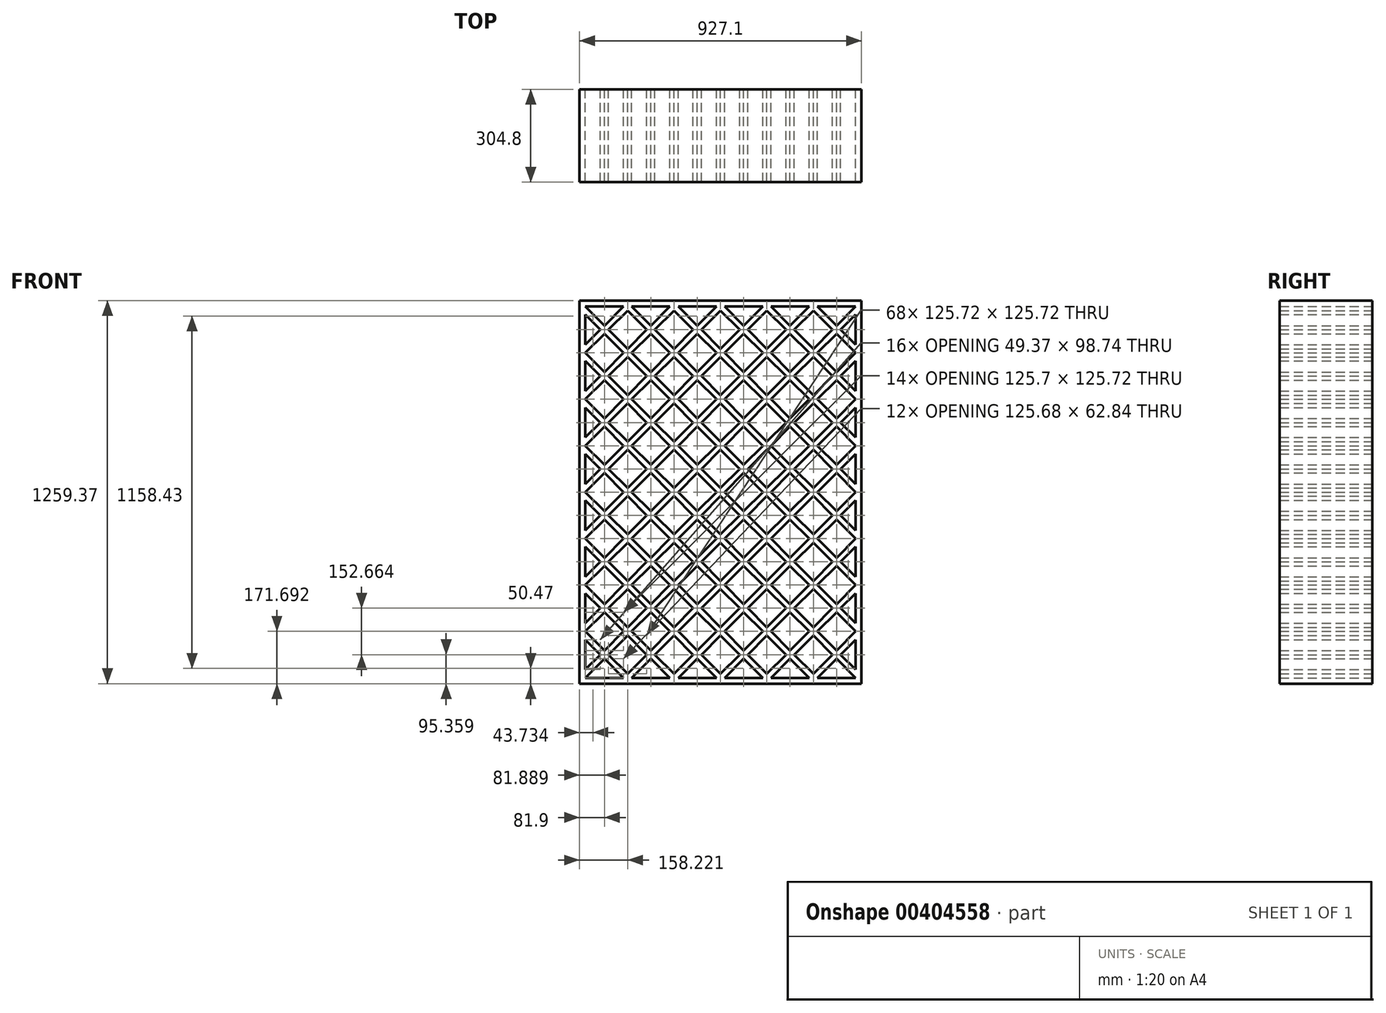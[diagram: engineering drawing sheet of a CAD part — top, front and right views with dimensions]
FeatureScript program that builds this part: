
annotation { "Feature Type Name" : "Feature", "Feature Type Description" : "" }
export const myFeature = defineFeature(function(context is Context, id is Id, definition is map)
    precondition{}
    {
        {
            var Q0;
            Q0=qCreatedBy(makeId("Front.planeOp"),FACE);
            var sketch = newSketch(context, id + "F0", { "sketchPlane" : qUnion([Q0])});
            skLineSegment(sketch, "E0.bottom", {"start": v(0, 0) * mm, "end": v(889, 0) * mm});
            skLineSegment(sketch, "E0.left", {"start": v(0, 0) * mm, "end": v(0, 1221.27) * mm});
            skLineSegment(sketch, "E0.right", {"start": v(889, 0) * mm, "end": v(889, 1221.27) * mm});
            skLineSegment(sketch, "E1", {"start": v(0, 0) * mm, "end": v(889, 889) * mm});
            skLineSegment(sketch, "E2", {"start": v(0, 26.94) * mm, "end": v(889, 915.94) * mm});
            skLineSegment(sketch, "E3", {"start": v(0, 152.66) * mm, "end": v(889, 1041.66) * mm});
            skLineSegment(sketch, "E4", {"start": v(0, 179.6) * mm, "end": v(889, 1068.6) * mm});
            skLineSegment(sketch, "E5", {"start": v(0, 305.33) * mm, "end": v(889, 1194.33) * mm});
            skLineSegment(sketch, "E6", {"start": v(0, 332.27) * mm, "end": v(889, 1221.27) * mm});
            skLineSegment(sketch, "E7", {"start": v(0, 458) * mm, "end": v(763.3, 1221.3) * mm});
            skLineSegment(sketch, "E8", {"start": v(0, 484.93) * mm, "end": v(736.36, 1221.3) * mm});
            skLineSegment(sketch, "E9", {"start": v(0, 610.66) * mm, "end": v(610.63, 1221.3) * mm});
            skLineSegment(sketch, "E10", {"start": v(0, 637.6) * mm, "end": v(583.7, 1221.3) * mm});
            skLineSegment(sketch, "E11", {"start": v(0, 763.32) * mm, "end": v(457.97, 1221.3) * mm});
            skLineSegment(sketch, "E12", {"start": v(0, 790.26) * mm, "end": v(431.03, 1221.3) * mm});
            skLineSegment(sketch, "E13", {"start": v(0, 915.99) * mm, "end": v(305.3, 1221.3) * mm});
            skLineSegment(sketch, "E14", {"start": v(0, 942.93) * mm, "end": v(278.37, 1221.3) * mm});
            skLineSegment(sketch, "E15", {"start": v(0, 1068.65) * mm, "end": v(152.64, 1221.3) * mm});
            skLineSegment(sketch, "E16", {"start": v(0, 1095.6) * mm, "end": v(125.7, 1221.3) * mm});
            skLineSegment(sketch, "E17", {"start": v(125.72, 0) * mm, "end": v(889, 763.28) * mm});
            skLineSegment(sketch, "E18", {"start": v(152.66, 0) * mm, "end": v(889, 736.34) * mm});
            skLineSegment(sketch, "E19", {"start": v(278.39, 0) * mm, "end": v(889, 610.61) * mm});
            skLineSegment(sketch, "E20", {"start": v(305.33, 0) * mm, "end": v(889, 583.67) * mm});
            skLineSegment(sketch, "E21", {"start": v(431.05, 0) * mm, "end": v(889, 457.95) * mm});
            skLineSegment(sketch, "E22", {"start": v(458, 0) * mm, "end": v(889, 431) * mm});
            skLineSegment(sketch, "E23", {"start": v(889, 0) * mm, "end": v(0, 889) * mm});
            skLineSegment(sketch, "E24", {"start": v(889, 26.94) * mm, "end": v(0, 915.94) * mm});
            skLineSegment(sketch, "E25", {"start": v(889, 152.66) * mm, "end": v(0, 1041.66) * mm});
            skLineSegment(sketch, "E26", {"start": v(889, 179.6) * mm, "end": v(0, 1068.6) * mm});
            skLineSegment(sketch, "E27", {"start": v(889, 305.33) * mm, "end": v(0, 1194.33) * mm});
            skLineSegment(sketch, "E28", {"start": v(889, 332.27) * mm, "end": v(0, 1221.27) * mm});
            skLineSegment(sketch, "E29", {"start": v(889, 458) * mm, "end": v(125.7, 1221.3) * mm});
            skLineSegment(sketch, "E30", {"start": v(889, 484.93) * mm, "end": v(152.64, 1221.3) * mm});
            skLineSegment(sketch, "E31", {"start": v(889, 610.66) * mm, "end": v(278.37, 1221.3) * mm});
            skLineSegment(sketch, "E32", {"start": v(889, 637.6) * mm, "end": v(305.3, 1221.3) * mm});
            skLineSegment(sketch, "E33", {"start": v(889, 763.32) * mm, "end": v(431.03, 1221.3) * mm});
            skLineSegment(sketch, "E34", {"start": v(889, 790.26) * mm, "end": v(457.97, 1221.3) * mm});
            skLineSegment(sketch, "E35", {"start": v(889, 915.99) * mm, "end": v(583.7, 1221.3) * mm});
            skLineSegment(sketch, "E36", {"start": v(889, 942.93) * mm, "end": v(610.63, 1221.3) * mm});
            skLineSegment(sketch, "E37", {"start": v(889, 1068.65) * mm, "end": v(736.36, 1221.3) * mm});
            skLineSegment(sketch, "E38", {"start": v(889, 1095.6) * mm, "end": v(763.3, 1221.3) * mm});
            skLineSegment(sketch, "E39", {"start": v(763.28, 0) * mm, "end": v(0, 763.28) * mm});
            skLineSegment(sketch, "E40", {"start": v(736.34, 0) * mm, "end": v(0, 736.34) * mm});
            skLineSegment(sketch, "E41", {"start": v(610.61, 0) * mm, "end": v(0, 610.61) * mm});
            skLineSegment(sketch, "E42", {"start": v(583.67, 0) * mm, "end": v(0, 583.67) * mm});
            skLineSegment(sketch, "E43", {"start": v(457.95, 0) * mm, "end": v(0, 457.95) * mm});
            skLineSegment(sketch, "E44", {"start": v(431, 0) * mm, "end": v(0, 431) * mm});
            skLineSegment(sketch, "E45", {"start": v(583.72, 0) * mm, "end": v(889, 305.28) * mm});
            skLineSegment(sketch, "E46", {"start": v(610.66, 0) * mm, "end": v(889, 278.34) * mm});
            skLineSegment(sketch, "E47", {"start": v(736.38, 0) * mm, "end": v(889, 152.62) * mm});
            skLineSegment(sketch, "E48", {"start": v(763.32, 0) * mm, "end": v(889, 125.68) * mm});
            skLineSegment(sketch, "E49", {"start": v(305.28, 0) * mm, "end": v(0, 305.28) * mm});
            skLineSegment(sketch, "E50", {"start": v(278.34, 0) * mm, "end": v(0, 278.34) * mm});
            skLineSegment(sketch, "E51", {"start": v(152.62, 0) * mm, "end": v(0, 152.62) * mm});
            skLineSegment(sketch, "E52", {"start": v(125.68, 0) * mm, "end": v(0, 125.68) * mm});
            skLineSegment(sketch, "E53", {"start": v(0, 1221.27) * mm, "end": v(889, 1221.27) * mm});
            skLineSegment(sketch, "E54.bottom", {"start": v(-19.05, -19.05) * mm, "end": v(908.05, -19.05) * mm});
            skLineSegment(sketch, "E54.left", {"start": v(-19.05, -19.05) * mm, "end": v(-19.05, 1240.32) * mm});
            skLineSegment(sketch, "E54.right", {"start": v(908.05, -19.05) * mm, "end": v(908.05, 1240.32) * mm});
            skLineSegment(sketch, "E55", {"start": v(-19.05, 1240.32) * mm, "end": v(908.05, 1240.32) * mm});
            skSolve(sketch);
        }
        {
            var Q0;
            Q0=makeQuery(id+"F0.imprint","IMPRINT",FACE,{"disambiguationData":[TD([[makeQuery(id+"F0.imprint","IMPRINT",EDGE,{"derivedFrom":sQuery(id+"F0.wireOp",EDGE,"E54.bottom")}),1.0]])]});
            var Q1;
            {var subQ0=sQuery(id+"F0.wireOp",EDGE,"E25");var subQ1=sQuery(id+"F0.wireOp",EDGE,"E11");var subQ2=makeQuery(id+"F0.imprint","INTERSECT",VERTEX,{"derivedFrom":[subQ1,subQ0]});Q1=makeQuery(id+"F0.imprint","IMPRINT",FACE,{"disambiguationData":[TD([[makeQuery(id+"F0.imprint","IMPRINT",EDGE,{"disambiguationData":[TD([[subQ2,-1.0]])],"derivedFrom":subQ1}),1.0]])]});}
            var Q2;
            {var subQ0=sQuery(id+"F0.wireOp",EDGE,"E27");var subQ1=sQuery(id+"F0.wireOp",EDGE,"E13");var subQ2=makeQuery(id+"F0.imprint","INTERSECT",VERTEX,{"derivedFrom":[subQ1,subQ0]});Q2=makeQuery(id+"F0.imprint","IMPRINT",FACE,{"disambiguationData":[TD([[makeQuery(id+"F0.imprint","IMPRINT",EDGE,{"disambiguationData":[TD([[subQ2,-1.0]])],"derivedFrom":subQ1}),1.0]])]});}
            var Q3;
            {var subQ0=sQuery(id+"F0.wireOp",EDGE,"E30");var subQ1=sQuery(id+"F0.wireOp",EDGE,"E11");var subQ2=makeQuery(id+"F0.imprint","INTERSECT",VERTEX,{"derivedFrom":[subQ1,subQ0]});Q3=makeQuery(id+"F0.imprint","IMPRINT",FACE,{"disambiguationData":[TD([[makeQuery(id+"F0.imprint","IMPRINT",EDGE,{"disambiguationData":[TD([[subQ2,-1.0]])],"derivedFrom":subQ1}),1.0]])]});}
            var Q4;
            {var subQ0=sQuery(id+"F0.wireOp",EDGE,"E23");var subQ1=sQuery(id+"F0.wireOp",EDGE,"E9");var subQ2=makeQuery(id+"F0.imprint","INTERSECT",VERTEX,{"derivedFrom":[subQ1,subQ0]});Q4=makeQuery(id+"F0.imprint","IMPRINT",FACE,{"disambiguationData":[TD([[makeQuery(id+"F0.imprint","IMPRINT",EDGE,{"disambiguationData":[TD([[subQ2,-1.0]])],"derivedFrom":subQ1}),1.0]])]});}
            var Q5;
            {var subQ0=sQuery(id+"F0.wireOp",EDGE,"E26");var subQ1=sQuery(id+"F0.wireOp",EDGE,"E7");var subQ2=makeQuery(id+"F0.imprint","INTERSECT",VERTEX,{"derivedFrom":[subQ1,subQ0]});Q5=makeQuery(id+"F0.imprint","IMPRINT",FACE,{"disambiguationData":[TD([[makeQuery(id+"F0.imprint","IMPRINT",EDGE,{"disambiguationData":[TD([[subQ2,-1.0]])],"derivedFrom":subQ1}),1.0]])]});}
            var Q6;
            {var subQ0=sQuery(id+"F0.wireOp",EDGE,"E27");var subQ1=sQuery(id+"F0.wireOp",EDGE,"E8");var subQ2=makeQuery(id+"F0.imprint","INTERSECT",VERTEX,{"derivedFrom":[subQ1,subQ0]});Q6=makeQuery(id+"F0.imprint","IMPRINT",FACE,{"disambiguationData":[TD([[makeQuery(id+"F0.imprint","IMPRINT",EDGE,{"disambiguationData":[TD([[subQ2,-1.0]])],"derivedFrom":subQ1}),1.0]])]});}
            var Q7;
            {var subQ0=sQuery(id+"F0.wireOp",EDGE,"E29");var subQ1=sQuery(id+"F0.wireOp",EDGE,"E9");var subQ2=makeQuery(id+"F0.imprint","INTERSECT",VERTEX,{"derivedFrom":[subQ1,subQ0]});Q7=makeQuery(id+"F0.imprint","IMPRINT",FACE,{"disambiguationData":[TD([[makeQuery(id+"F0.imprint","IMPRINT",EDGE,{"disambiguationData":[TD([[subQ2,-1.0]])],"derivedFrom":subQ1}),1.0]])]});}
            var Q8;
            {var subQ0=sQuery(id+"F0.wireOp",EDGE,"E24");var subQ1=sQuery(id+"F0.wireOp",EDGE,"E11");var subQ2=makeQuery(id+"F0.imprint","INTERSECT",VERTEX,{"derivedFrom":[subQ1,subQ0]});Q8=makeQuery(id+"F0.imprint","IMPRINT",FACE,{"disambiguationData":[TD([[makeQuery(id+"F0.imprint","IMPRINT",EDGE,{"disambiguationData":[TD([[subQ2,-1.0]])],"derivedFrom":subQ1}),1.0]])]});}
            var Q9;
            {var subQ0=sQuery(id+"F0.wireOp",EDGE,"E27");var subQ1=sQuery(id+"F0.wireOp",EDGE,"E15");var subQ2=makeQuery(id+"F0.imprint","INTERSECT",VERTEX,{"derivedFrom":[subQ1,subQ0]});Q9=makeQuery(id+"F0.imprint","IMPRINT",FACE,{"disambiguationData":[TD([[makeQuery(id+"F0.imprint","IMPRINT",EDGE,{"disambiguationData":[TD([[subQ2,-1.0]])],"derivedFrom":subQ1}),1.0]])]});}
            var Q10;
            {var subQ0=sQuery(id+"F0.wireOp",EDGE,"E27");var subQ1=sQuery(id+"F0.wireOp",EDGE,"E10");var subQ2=makeQuery(id+"F0.imprint","INTERSECT",VERTEX,{"derivedFrom":[subQ1,subQ0]});Q10=makeQuery(id+"F0.imprint","IMPRINT",FACE,{"disambiguationData":[TD([[makeQuery(id+"F0.imprint","IMPRINT",EDGE,{"disambiguationData":[TD([[subQ2,-1.0]])],"derivedFrom":subQ1}),1.0]])]});}
            var Q11;
            {var subQ0=sQuery(id+"F0.wireOp",EDGE,"E29");var subQ1=sQuery(id+"F0.wireOp",EDGE,"E11");var subQ2=makeQuery(id+"F0.imprint","INTERSECT",VERTEX,{"derivedFrom":[subQ1,subQ0]});Q11=makeQuery(id+"F0.imprint","IMPRINT",FACE,{"disambiguationData":[TD([[makeQuery(id+"F0.imprint","IMPRINT",EDGE,{"disambiguationData":[TD([[subQ2,-1.0]])],"derivedFrom":subQ1}),1.0]])]});}
            var Q12;
            {var subQ0=sQuery(id+"F0.wireOp",EDGE,"E23");var subQ1=sQuery(id+"F0.wireOp",EDGE,"E10");var subQ2=makeQuery(id+"F0.imprint","INTERSECT",VERTEX,{"derivedFrom":[subQ1,subQ0]});Q12=makeQuery(id+"F0.imprint","IMPRINT",FACE,{"disambiguationData":[TD([[makeQuery(id+"F0.imprint","IMPRINT",EDGE,{"disambiguationData":[TD([[subQ2,-1.0]])],"derivedFrom":subQ1}),1.0]])]});}
            var Q13;
            {var subQ0=sQuery(id+"F0.wireOp",EDGE,"E25");var subQ1=sQuery(id+"F0.wireOp",EDGE,"E13");var subQ2=makeQuery(id+"F0.imprint","INTERSECT",VERTEX,{"derivedFrom":[subQ1,subQ0]});Q13=makeQuery(id+"F0.imprint","IMPRINT",FACE,{"disambiguationData":[TD([[makeQuery(id+"F0.imprint","IMPRINT",EDGE,{"disambiguationData":[TD([[subQ2,-1.0]])],"derivedFrom":subQ1}),1.0]])]});}
            var Q14;
            {var subQ0=sQuery(id+"F0.wireOp",EDGE,"E25");var subQ1=sQuery(id+"F0.wireOp",EDGE,"E8");var subQ2=makeQuery(id+"F0.imprint","INTERSECT",VERTEX,{"derivedFrom":[subQ1,subQ0]});Q14=makeQuery(id+"F0.imprint","IMPRINT",FACE,{"disambiguationData":[TD([[makeQuery(id+"F0.imprint","IMPRINT",EDGE,{"disambiguationData":[TD([[subQ2,-1.0]])],"derivedFrom":subQ1}),1.0]])]});}
            var Q15;
            {var subQ0=sQuery(id+"F0.wireOp",EDGE,"E27");var subQ1=sQuery(id+"F0.wireOp",EDGE,"E9");var subQ2=makeQuery(id+"F0.imprint","INTERSECT",VERTEX,{"derivedFrom":[subQ1,subQ0]});Q15=makeQuery(id+"F0.imprint","IMPRINT",FACE,{"disambiguationData":[TD([[makeQuery(id+"F0.imprint","IMPRINT",EDGE,{"disambiguationData":[TD([[subQ2,-1.0]])],"derivedFrom":subQ1}),1.0]])]});}
            var Q16;
            {var subQ0=sQuery(id+"F0.wireOp",EDGE,"E31");var subQ1=sQuery(id+"F0.wireOp",EDGE,"E11");var subQ2=makeQuery(id+"F0.imprint","INTERSECT",VERTEX,{"derivedFrom":[subQ1,subQ0]});Q16=makeQuery(id+"F0.imprint","IMPRINT",FACE,{"disambiguationData":[TD([[makeQuery(id+"F0.imprint","IMPRINT",EDGE,{"disambiguationData":[TD([[subQ2,-1.0]])],"derivedFrom":subQ1}),1.0]])]});}
            var Q17;
            {var subQ0=sQuery(id+"F0.wireOp",EDGE,"E25");var subQ1=sQuery(id+"F0.wireOp",EDGE,"E10");var subQ2=makeQuery(id+"F0.imprint","INTERSECT",VERTEX,{"derivedFrom":[subQ1,subQ0]});Q17=makeQuery(id+"F0.imprint","IMPRINT",FACE,{"disambiguationData":[TD([[makeQuery(id+"F0.imprint","IMPRINT",EDGE,{"disambiguationData":[TD([[subQ2,-1.0]])],"derivedFrom":subQ1}),1.0]])]});}
            var Q18;
            {var subQ0=sQuery(id+"F0.wireOp",EDGE,"E25");var subQ1=sQuery(id+"F0.wireOp",EDGE,"E12");var subQ2=makeQuery(id+"F0.imprint","INTERSECT",VERTEX,{"derivedFrom":[subQ1,subQ0]});Q18=makeQuery(id+"F0.imprint","IMPRINT",FACE,{"disambiguationData":[TD([[makeQuery(id+"F0.imprint","IMPRINT",EDGE,{"disambiguationData":[TD([[subQ2,-1.0]])],"derivedFrom":subQ1}),1.0]])]});}
            var Q19;
            {var subQ0=sQuery(id+"F0.wireOp",EDGE,"E28");var subQ1=sQuery(id+"F0.wireOp",EDGE,"E11");var subQ2=makeQuery(id+"F0.imprint","INTERSECT",VERTEX,{"derivedFrom":[subQ1,subQ0]});Q19=makeQuery(id+"F0.imprint","IMPRINT",FACE,{"disambiguationData":[TD([[makeQuery(id+"F0.imprint","IMPRINT",EDGE,{"disambiguationData":[TD([[subQ2,-1.0]])],"derivedFrom":subQ1}),1.0]])]});}
            var Q20;
            {var subQ0=sQuery(id+"F0.wireOp",EDGE,"E26");var subQ1=sQuery(id+"F0.wireOp",EDGE,"E9");var subQ2=makeQuery(id+"F0.imprint","INTERSECT",VERTEX,{"derivedFrom":[subQ1,subQ0]});Q20=makeQuery(id+"F0.imprint","IMPRINT",FACE,{"disambiguationData":[TD([[makeQuery(id+"F0.imprint","IMPRINT",EDGE,{"disambiguationData":[TD([[subQ2,-1.0]])],"derivedFrom":subQ1}),1.0]])]});}
            var Q21;
            {var subQ0=sQuery(id+"F0.wireOp",EDGE,"E25");var subQ1=sQuery(id+"F0.wireOp",EDGE,"E7");var subQ2=makeQuery(id+"F0.imprint","INTERSECT",VERTEX,{"derivedFrom":[subQ1,subQ0]});Q21=makeQuery(id+"F0.imprint","IMPRINT",FACE,{"disambiguationData":[TD([[makeQuery(id+"F0.imprint","IMPRINT",EDGE,{"disambiguationData":[TD([[subQ2,-1.0]])],"derivedFrom":subQ1}),1.0]])]});}
            var Q22;
            {var subQ0=sQuery(id+"F0.wireOp",EDGE,"E28");var subQ1=sQuery(id+"F0.wireOp",EDGE,"E9");var subQ2=makeQuery(id+"F0.imprint","INTERSECT",VERTEX,{"derivedFrom":[subQ1,subQ0]});Q22=makeQuery(id+"F0.imprint","IMPRINT",FACE,{"disambiguationData":[TD([[makeQuery(id+"F0.imprint","IMPRINT",EDGE,{"disambiguationData":[TD([[subQ2,-1.0]])],"derivedFrom":subQ1}),1.0]])]});}
            var Q23;
            {var subQ0=sQuery(id+"F0.wireOp",EDGE,"E23");var subQ1=sQuery(id+"F0.wireOp",EDGE,"E11");var subQ2=makeQuery(id+"F0.imprint","INTERSECT",VERTEX,{"derivedFrom":[subQ1,subQ0]});Q23=makeQuery(id+"F0.imprint","IMPRINT",FACE,{"disambiguationData":[TD([[makeQuery(id+"F0.imprint","IMPRINT",EDGE,{"disambiguationData":[TD([[subQ2,-1.0]])],"derivedFrom":subQ1}),1.0]])]});}
            var Q24;
            {var subQ0=sQuery(id+"F0.wireOp",EDGE,"E26");var subQ1=sQuery(id+"F0.wireOp",EDGE,"E13");var subQ2=makeQuery(id+"F0.imprint","INTERSECT",VERTEX,{"derivedFrom":[subQ1,subQ0]});Q24=makeQuery(id+"F0.imprint","IMPRINT",FACE,{"disambiguationData":[TD([[makeQuery(id+"F0.imprint","IMPRINT",EDGE,{"disambiguationData":[TD([[subQ2,-1.0]])],"derivedFrom":subQ1}),1.0]])]});}
            var Q25;
            {var subQ0=sQuery(id+"F0.wireOp",EDGE,"E27");var subQ1=sQuery(id+"F0.wireOp",EDGE,"E14");var subQ2=makeQuery(id+"F0.imprint","INTERSECT",VERTEX,{"derivedFrom":[subQ1,subQ0]});Q25=makeQuery(id+"F0.imprint","IMPRINT",FACE,{"disambiguationData":[TD([[makeQuery(id+"F0.imprint","IMPRINT",EDGE,{"disambiguationData":[TD([[subQ2,-1.0]])],"derivedFrom":subQ1}),1.0]])]});}
            var Q26;
            {var subQ0=sQuery(id+"F0.wireOp",EDGE,"E27");var subQ1=sQuery(id+"F0.wireOp",EDGE,"E11");var subQ2=makeQuery(id+"F0.imprint","INTERSECT",VERTEX,{"derivedFrom":[subQ1,subQ0]});Q26=makeQuery(id+"F0.imprint","IMPRINT",FACE,{"disambiguationData":[TD([[makeQuery(id+"F0.imprint","IMPRINT",EDGE,{"disambiguationData":[TD([[subQ2,-1.0]])],"derivedFrom":subQ1}),1.0]])]});}
            var Q27;
            {var subQ0=sQuery(id+"F0.wireOp",EDGE,"E25");var subQ1=sQuery(id+"F0.wireOp",EDGE,"E9");var subQ2=makeQuery(id+"F0.imprint","INTERSECT",VERTEX,{"derivedFrom":[subQ1,subQ0]});Q27=makeQuery(id+"F0.imprint","IMPRINT",FACE,{"disambiguationData":[TD([[makeQuery(id+"F0.imprint","IMPRINT",EDGE,{"disambiguationData":[TD([[subQ2,-1.0]])],"derivedFrom":subQ1}),1.0]])]});}
            var Q28;
            {var subQ0=sQuery(id+"F0.wireOp",EDGE,"E29");var subQ1=sQuery(id+"F0.wireOp",EDGE,"E13");var subQ2=makeQuery(id+"F0.imprint","INTERSECT",VERTEX,{"derivedFrom":[subQ1,subQ0]});Q28=makeQuery(id+"F0.imprint","IMPRINT",FACE,{"disambiguationData":[TD([[makeQuery(id+"F0.imprint","IMPRINT",EDGE,{"disambiguationData":[TD([[subQ2,-1.0]])],"derivedFrom":subQ1}),1.0]])]});}
            var Q29;
            {var subQ0=sQuery(id+"F0.wireOp",EDGE,"E26");var subQ1=sQuery(id+"F0.wireOp",EDGE,"E11");var subQ2=makeQuery(id+"F0.imprint","INTERSECT",VERTEX,{"derivedFrom":[subQ1,subQ0]});Q29=makeQuery(id+"F0.imprint","IMPRINT",FACE,{"disambiguationData":[TD([[makeQuery(id+"F0.imprint","IMPRINT",EDGE,{"disambiguationData":[TD([[subQ2,-1.0]])],"derivedFrom":subQ1}),1.0]])]});}
            var Q30;
            {var subQ0=sQuery(id+"F0.wireOp",EDGE,"E27");var subQ1=sQuery(id+"F0.wireOp",EDGE,"E12");var subQ2=makeQuery(id+"F0.imprint","INTERSECT",VERTEX,{"derivedFrom":[subQ1,subQ0]});Q30=makeQuery(id+"F0.imprint","IMPRINT",FACE,{"disambiguationData":[TD([[makeQuery(id+"F0.imprint","IMPRINT",EDGE,{"disambiguationData":[TD([[subQ2,-1.0]])],"derivedFrom":subQ1}),1.0]])]});}
            var Q31;
            {var subQ0=sQuery(id+"F0.wireOp",EDGE,"E28");var subQ1=sQuery(id+"F0.wireOp",EDGE,"E13");var subQ2=makeQuery(id+"F0.imprint","INTERSECT",VERTEX,{"derivedFrom":[subQ1,subQ0]});Q31=makeQuery(id+"F0.imprint","IMPRINT",FACE,{"disambiguationData":[TD([[makeQuery(id+"F0.imprint","IMPRINT",EDGE,{"disambiguationData":[TD([[subQ2,-1.0]])],"derivedFrom":subQ1}),1.0]])]});}
            var Q32;
            {var subQ0=sQuery(id+"F0.wireOp",EDGE,"E27");var subQ1=sQuery(id+"F0.wireOp",EDGE,"E7");var subQ2=makeQuery(id+"F0.imprint","INTERSECT",VERTEX,{"derivedFrom":[subQ1,subQ0]});Q32=makeQuery(id+"F0.imprint","IMPRINT",FACE,{"disambiguationData":[TD([[makeQuery(id+"F0.imprint","IMPRINT",EDGE,{"disambiguationData":[TD([[subQ2,-1.0]])],"derivedFrom":subQ1}),1.0]])]});}
            var Q33;
            {var subQ0=sQuery(id+"F0.wireOp",EDGE,"E29");var subQ1=sQuery(id+"F0.wireOp",EDGE,"E12");var subQ2=makeQuery(id+"F0.imprint","INTERSECT",VERTEX,{"derivedFrom":[subQ1,subQ0]});Q33=makeQuery(id+"F0.imprint","IMPRINT",FACE,{"disambiguationData":[TD([[makeQuery(id+"F0.imprint","IMPRINT",EDGE,{"disambiguationData":[TD([[subQ2,-1.0]])],"derivedFrom":subQ1}),1.0]])]});}
            var Q34;
            {var subQ0=sQuery(id+"F0.wireOp",EDGE,"E29");var subQ1=sQuery(id+"F0.wireOp",EDGE,"E10");var subQ2=makeQuery(id+"F0.imprint","INTERSECT",VERTEX,{"derivedFrom":[subQ1,subQ0]});Q34=makeQuery(id+"F0.imprint","IMPRINT",FACE,{"disambiguationData":[TD([[makeQuery(id+"F0.imprint","IMPRINT",EDGE,{"disambiguationData":[TD([[subQ2,-1.0]])],"derivedFrom":subQ1}),1.0]])]});}
            var Q35;
            {var subQ0=sQuery(id+"F0.wireOp",EDGE,"E24");var subQ1=sQuery(id+"F0.wireOp",EDGE,"E9");var subQ2=makeQuery(id+"F0.imprint","INTERSECT",VERTEX,{"derivedFrom":[subQ1,subQ0]});Q35=makeQuery(id+"F0.imprint","IMPRINT",FACE,{"disambiguationData":[TD([[makeQuery(id+"F0.imprint","IMPRINT",EDGE,{"disambiguationData":[TD([[subQ2,-1.0]])],"derivedFrom":subQ1}),1.0]])]});}
            var Q36;
            {var subQ0=sQuery(id+"F0.wireOp",EDGE,"E42");var subQ1=sQuery(id+"F0.wireOp",EDGE,"E4");var subQ2=makeQuery(id+"F0.imprint","INTERSECT",VERTEX,{"derivedFrom":[subQ1,subQ0]});Q36=makeQuery(id+"F0.imprint","IMPRINT",FACE,{"disambiguationData":[TD([[makeQuery(id+"F0.imprint","IMPRINT",EDGE,{"disambiguationData":[TD([[subQ2,-1.0]])],"derivedFrom":subQ1}),1.0]])]});}
            var Q37;
            {var subQ0=sQuery(id+"F0.wireOp",EDGE,"E43");var subQ1=sQuery(id+"F0.wireOp",EDGE,"E19");var subQ2=makeQuery(id+"F0.imprint","INTERSECT",VERTEX,{"derivedFrom":[subQ1,subQ0]});Q37=makeQuery(id+"F0.imprint","IMPRINT",FACE,{"disambiguationData":[TD([[makeQuery(id+"F0.imprint","IMPRINT",EDGE,{"disambiguationData":[TD([[subQ2,-1.0]])],"derivedFrom":subQ1}),-1.0]])]});}
            var Q38;
            {var subQ0=sQuery(id+"F0.wireOp",EDGE,"E35");var subQ1=sQuery(id+"F0.wireOp",EDGE,"E4");var subQ2=makeQuery(id+"F0.imprint","INTERSECT",VERTEX,{"derivedFrom":[subQ1,subQ0]});Q38=makeQuery(id+"F0.imprint","IMPRINT",FACE,{"disambiguationData":[TD([[makeQuery(id+"F0.imprint","IMPRINT",EDGE,{"disambiguationData":[TD([[subQ2,-1.0]])],"derivedFrom":subQ1}),1.0]])]});}
            var Q39;
            {var subQ0=sQuery(id+"F0.wireOp",EDGE,"E32");var subQ1=sQuery(id+"F0.wireOp",EDGE,"E5");var subQ2=makeQuery(id+"F0.imprint","INTERSECT",VERTEX,{"derivedFrom":[subQ1,subQ0]});Q39=makeQuery(id+"F0.imprint","IMPRINT",FACE,{"disambiguationData":[TD([[makeQuery(id+"F0.imprint","IMPRINT",EDGE,{"disambiguationData":[TD([[subQ2,-1.0]])],"derivedFrom":subQ1}),1.0]])]});}
            var Q40;
            {var subQ0=sQuery(id+"F0.wireOp",EDGE,"E29");var subQ1=sQuery(id+"F0.wireOp",EDGE,"E6");var subQ2=makeQuery(id+"F0.imprint","INTERSECT",VERTEX,{"derivedFrom":[subQ1,subQ0]});Q40=makeQuery(id+"F0.imprint","IMPRINT",FACE,{"disambiguationData":[TD([[makeQuery(id+"F0.imprint","IMPRINT",EDGE,{"disambiguationData":[TD([[subQ2,-1.0]])],"derivedFrom":subQ1}),1.0]])]});}
            var Q41;
            {var subQ0=sQuery(id+"F0.wireOp",EDGE,"E40");var subQ1=sQuery(id+"F0.wireOp",EDGE,"E22");var subQ2=makeQuery(id+"F0.imprint","INTERSECT",VERTEX,{"derivedFrom":[subQ1,subQ0]});Q41=makeQuery(id+"F0.imprint","IMPRINT",FACE,{"disambiguationData":[TD([[makeQuery(id+"F0.imprint","IMPRINT",EDGE,{"disambiguationData":[TD([[subQ2,-1.0]])],"derivedFrom":subQ1}),-1.0]])]});}
            var Q42;
            {var subQ3=sQuery(id+"F0.wireOp",EDGE,"E20");var subQ5=sQuery(id+"F0.wireOp",EDGE,"E0.bottom");var subQ6=makeQuery(id+"F0.imprint","INTERSECT",VERTEX,{"derivedFrom":[subQ5,subQ3]});Q42=makeQuery(id+"F0.imprint","IMPRINT",FACE,{"disambiguationData":[TD([[makeQuery(id+"F0.imprint","IMPRINT",EDGE,{"disambiguationData":[TD([[subQ6,1.0]])],"derivedFrom":subQ5}),1.0]])]});}
            var Q43;
            {var subQ0=sQuery(id+"F0.wireOp",EDGE,"E39");var subQ1=sQuery(id+"F0.wireOp",EDGE,"E1");var subQ2=makeQuery(id+"F0.imprint","INTERSECT",VERTEX,{"derivedFrom":[subQ1,subQ0]});Q43=makeQuery(id+"F0.imprint","IMPRINT",FACE,{"disambiguationData":[TD([[makeQuery(id+"F0.imprint","IMPRINT",EDGE,{"disambiguationData":[TD([[subQ2,-1.0]])],"derivedFrom":subQ1}),1.0]])]});}
            var Q44;
            {var subQ0=sQuery(id+"F0.wireOp",EDGE,"E39");var subQ1=sQuery(id+"F0.wireOp",EDGE,"E19");var subQ2=makeQuery(id+"F0.imprint","INTERSECT",VERTEX,{"derivedFrom":[subQ1,subQ0]});Q44=makeQuery(id+"F0.imprint","IMPRINT",FACE,{"disambiguationData":[TD([[makeQuery(id+"F0.imprint","IMPRINT",EDGE,{"disambiguationData":[TD([[subQ2,-1.0]])],"derivedFrom":subQ1}),-1.0]])]});}
            var Q45;
            {var subQ0=sQuery(id+"F0.wireOp",EDGE,"E30");var subQ1=sQuery(id+"F0.wireOp",EDGE,"E1");var subQ2=makeQuery(id+"F0.imprint","INTERSECT",VERTEX,{"derivedFrom":[subQ1,subQ0]});Q45=makeQuery(id+"F0.imprint","IMPRINT",FACE,{"disambiguationData":[TD([[makeQuery(id+"F0.imprint","IMPRINT",EDGE,{"disambiguationData":[TD([[subQ2,-1.0]])],"derivedFrom":subQ1}),1.0]])]});}
            var Q46;
            {var subQ0=sQuery(id+"F0.wireOp",EDGE,"E25");var subQ1=sQuery(id+"F0.wireOp",EDGE,"E2");var subQ2=makeQuery(id+"F0.imprint","INTERSECT",VERTEX,{"derivedFrom":[subQ1,subQ0]});Q46=makeQuery(id+"F0.imprint","IMPRINT",FACE,{"disambiguationData":[TD([[makeQuery(id+"F0.imprint","IMPRINT",EDGE,{"disambiguationData":[TD([[subQ2,-1.0]])],"derivedFrom":subQ1}),1.0]])]});}
            var Q47;
            {var subQ0=sQuery(id+"F0.wireOp",EDGE,"E39");var subQ1=sQuery(id+"F0.wireOp",EDGE,"E3");var subQ2=makeQuery(id+"F0.imprint","INTERSECT",VERTEX,{"derivedFrom":[subQ1,subQ0]});Q47=makeQuery(id+"F0.imprint","IMPRINT",FACE,{"disambiguationData":[TD([[makeQuery(id+"F0.imprint","IMPRINT",EDGE,{"disambiguationData":[TD([[subQ2,-1.0]])],"derivedFrom":subQ1}),1.0]])]});}
            var Q48;
            {var subQ0=sQuery(id+"F0.wireOp",EDGE,"E51");var subQ1=sQuery(id+"F0.wireOp",EDGE,"E0.left");var subQ2=makeQuery(id+"F0.imprint","INTERSECT",VERTEX,{"derivedFrom":[subQ1,subQ0]});Q48=makeQuery(id+"F0.imprint","IMPRINT",FACE,{"disambiguationData":[TD([[makeQuery(id+"F0.imprint","IMPRINT",EDGE,{"disambiguationData":[TD([[subQ2,1.0]])],"derivedFrom":subQ1}),-1.0]])]});}
            var Q49;
            {var subQ0=sQuery(id+"F0.wireOp",EDGE,"E47");var subQ1=sQuery(id+"F0.wireOp",EDGE,"E0.right");var subQ2=makeQuery(id+"F0.imprint","INTERSECT",VERTEX,{"derivedFrom":[subQ1,subQ0]});Q49=makeQuery(id+"F0.imprint","IMPRINT",FACE,{"disambiguationData":[TD([[makeQuery(id+"F0.imprint","IMPRINT",EDGE,{"disambiguationData":[TD([[subQ2,1.0]])],"derivedFrom":subQ1}),1.0]])]});}
            var Q50;
            {var subQ3=sQuery(id+"F0.wireOp",EDGE,"E39");var subQ5=sQuery(id+"F0.wireOp",EDGE,"E0.bottom");var subQ6=makeQuery(id+"F0.imprint","INTERSECT",VERTEX,{"derivedFrom":[subQ5,subQ3]});Q50=makeQuery(id+"F0.imprint","IMPRINT",FACE,{"disambiguationData":[TD([[makeQuery(id+"F0.imprint","IMPRINT",EDGE,{"disambiguationData":[TD([[subQ6,-1.0]])],"derivedFrom":subQ5}),1.0]])]});}
            var Q51;
            {var subQ0=sQuery(id+"F0.wireOp",EDGE,"E47");var subQ1=sQuery(id+"F0.wireOp",EDGE,"E23");var subQ2=makeQuery(id+"F0.imprint","INTERSECT",VERTEX,{"derivedFrom":[subQ1,subQ0]});Q51=makeQuery(id+"F0.imprint","IMPRINT",FACE,{"disambiguationData":[TD([[makeQuery(id+"F0.imprint","IMPRINT",EDGE,{"disambiguationData":[TD([[subQ2,-1.0]])],"derivedFrom":subQ1}),-1.0]])]});}
            var Q52;
            {var subQ0=sQuery(id+"F0.wireOp",EDGE,"E27");var subQ1=sQuery(id+"F0.wireOp",EDGE,"E5");var subQ2=makeQuery(id+"F0.imprint","INTERSECT",VERTEX,{"derivedFrom":[subQ1,subQ0]});Q52=makeQuery(id+"F0.imprint","IMPRINT",FACE,{"disambiguationData":[TD([[makeQuery(id+"F0.imprint","IMPRINT",EDGE,{"disambiguationData":[TD([[subQ2,-1.0]])],"derivedFrom":subQ1}),1.0]])]});}
            var Q53;
            {var subQ0=sQuery(id+"F0.wireOp",EDGE,"E51");var subQ1=sQuery(id+"F0.wireOp",EDGE,"E1");var subQ2=makeQuery(id+"F0.imprint","INTERSECT",VERTEX,{"derivedFrom":[subQ1,subQ0]});Q53=makeQuery(id+"F0.imprint","IMPRINT",FACE,{"disambiguationData":[TD([[makeQuery(id+"F0.imprint","IMPRINT",EDGE,{"disambiguationData":[TD([[subQ2,-1.0]])],"derivedFrom":subQ1}),1.0]])]});}
            var Q54;
            {var subQ0=sQuery(id+"F0.wireOp",EDGE,"E23");var subQ1=sQuery(id+"F0.wireOp",EDGE,"E21");var subQ2=makeQuery(id+"F0.imprint","INTERSECT",VERTEX,{"derivedFrom":[subQ1,subQ0]});Q54=makeQuery(id+"F0.imprint","IMPRINT",FACE,{"disambiguationData":[TD([[makeQuery(id+"F0.imprint","IMPRINT",EDGE,{"disambiguationData":[TD([[subQ2,-1.0]])],"derivedFrom":subQ1}),-1.0]])]});}
            var Q55;
            {var subQ0=sQuery(id+"F0.wireOp",EDGE,"E46");var subQ1=sQuery(id+"F0.wireOp",EDGE,"E24");var subQ2=makeQuery(id+"F0.imprint","INTERSECT",VERTEX,{"derivedFrom":[subQ1,subQ0]});Q55=makeQuery(id+"F0.imprint","IMPRINT",FACE,{"disambiguationData":[TD([[makeQuery(id+"F0.imprint","IMPRINT",EDGE,{"disambiguationData":[TD([[subQ2,-1.0]])],"derivedFrom":subQ1}),-1.0]])]});}
            var Q56;
            {var subQ0=sQuery(id+"F0.wireOp",EDGE,"E11");var subQ1=sQuery(id+"F0.wireOp",EDGE,"E0.left");var subQ2=makeQuery(id+"F0.imprint","INTERSECT",VERTEX,{"derivedFrom":[subQ1,subQ0]});Q56=makeQuery(id+"F0.imprint","IMPRINT",FACE,{"disambiguationData":[TD([[makeQuery(id+"F0.imprint","IMPRINT",EDGE,{"disambiguationData":[TD([[subQ2,-1.0]])],"derivedFrom":subQ1}),-1.0]])]});}
            var Q57;
            {var subQ1=sQuery(id+"F0.wireOp",EDGE,"E11");var subQ5=sQuery(id+"F0.wireOp",EDGE,"E32");var subQ6=makeQuery(id+"F0.imprint","INTERSECT",VERTEX,{"derivedFrom":[subQ1,subQ5]});Q57=makeQuery(id+"F0.imprint","IMPRINT",FACE,{"disambiguationData":[TD([[makeQuery(id+"F0.imprint","IMPRINT",EDGE,{"disambiguationData":[TD([[subQ6,-1.0]])],"derivedFrom":subQ1}),1.0]])]});}
            var Q58;
            {var subQ0=sQuery(id+"F0.wireOp",EDGE,"E50");var subQ1=sQuery(id+"F0.wireOp",EDGE,"E17");var subQ2=makeQuery(id+"F0.imprint","INTERSECT",VERTEX,{"derivedFrom":[subQ1,subQ0]});Q58=makeQuery(id+"F0.imprint","IMPRINT",FACE,{"disambiguationData":[TD([[makeQuery(id+"F0.imprint","IMPRINT",EDGE,{"disambiguationData":[TD([[subQ2,-1.0]])],"derivedFrom":subQ1}),-1.0]])]});}
            var Q59;
            {var subQ0=sQuery(id+"F0.wireOp",EDGE,"E25");var subQ1=sQuery(id+"F0.wireOp",EDGE,"E5");var subQ2=makeQuery(id+"F0.imprint","INTERSECT",VERTEX,{"derivedFrom":[subQ1,subQ0]});Q59=makeQuery(id+"F0.imprint","IMPRINT",FACE,{"disambiguationData":[TD([[makeQuery(id+"F0.imprint","IMPRINT",EDGE,{"disambiguationData":[TD([[subQ2,-1.0]])],"derivedFrom":subQ1}),1.0]])]});}
            var Q60;
            {var subQ0=sQuery(id+"F0.wireOp",EDGE,"E25");var subQ1=sQuery(id+"F0.wireOp",EDGE,"E17");var subQ2=makeQuery(id+"F0.imprint","INTERSECT",VERTEX,{"derivedFrom":[subQ1,subQ0]});Q60=makeQuery(id+"F0.imprint","IMPRINT",FACE,{"disambiguationData":[TD([[makeQuery(id+"F0.imprint","IMPRINT",EDGE,{"disambiguationData":[TD([[subQ2,-1.0]])],"derivedFrom":subQ1}),-1.0]])]});}
            var Q61;
            {var subQ0=sQuery(id+"F0.wireOp",EDGE,"E50");var subQ1=sQuery(id+"F0.wireOp",EDGE,"E3");var subQ2=makeQuery(id+"F0.imprint","INTERSECT",VERTEX,{"derivedFrom":[subQ1,subQ0]});Q61=makeQuery(id+"F0.imprint","IMPRINT",FACE,{"disambiguationData":[TD([[makeQuery(id+"F0.imprint","IMPRINT",EDGE,{"disambiguationData":[TD([[subQ2,-1.0]])],"derivedFrom":subQ1}),1.0]])]});}
            var Q62;
            {var subQ0=sQuery(id+"F0.wireOp",EDGE,"E40");var subQ1=sQuery(id+"F0.wireOp",EDGE,"E6");var subQ2=makeQuery(id+"F0.imprint","INTERSECT",VERTEX,{"derivedFrom":[subQ1,subQ0]});Q62=makeQuery(id+"F0.imprint","IMPRINT",FACE,{"disambiguationData":[TD([[makeQuery(id+"F0.imprint","IMPRINT",EDGE,{"disambiguationData":[TD([[subQ2,-1.0]])],"derivedFrom":subQ1}),1.0]])]});}
            var Q63;
            {var subQ0=sQuery(id+"F0.wireOp",EDGE,"E35");var subQ1=sQuery(id+"F0.wireOp",EDGE,"E7");var subQ2=makeQuery(id+"F0.imprint","INTERSECT",VERTEX,{"derivedFrom":[subQ1,subQ0]});Q63=makeQuery(id+"F0.imprint","IMPRINT",FACE,{"disambiguationData":[TD([[makeQuery(id+"F0.imprint","IMPRINT",EDGE,{"disambiguationData":[TD([[subQ2,-1.0]])],"derivedFrom":subQ1}),1.0]])]});}
            var Q64;
            {var subQ0=sQuery(id+"F0.wireOp",EDGE,"E39");var subQ1=sQuery(id+"F0.wireOp",EDGE,"E9");var subQ2=makeQuery(id+"F0.imprint","INTERSECT",VERTEX,{"derivedFrom":[subQ1,subQ0]});Q64=makeQuery(id+"F0.imprint","IMPRINT",FACE,{"disambiguationData":[TD([[makeQuery(id+"F0.imprint","IMPRINT",EDGE,{"disambiguationData":[TD([[subQ2,-1.0]])],"derivedFrom":subQ1}),1.0]])]});}
            var Q65;
            {var subQ0=sQuery(id+"F0.wireOp",EDGE,"E33");var subQ1=sQuery(id+"F0.wireOp",EDGE,"E2");var subQ2=makeQuery(id+"F0.imprint","INTERSECT",VERTEX,{"derivedFrom":[subQ1,subQ0]});Q65=makeQuery(id+"F0.imprint","IMPRINT",FACE,{"disambiguationData":[TD([[makeQuery(id+"F0.imprint","IMPRINT",EDGE,{"disambiguationData":[TD([[subQ2,-1.0]])],"derivedFrom":subQ1}),1.0]])]});}
            var Q66;
            {var subQ0=sQuery(id+"F0.wireOp",EDGE,"E30");var subQ1=sQuery(id+"F0.wireOp",EDGE,"E3");var subQ2=makeQuery(id+"F0.imprint","INTERSECT",VERTEX,{"derivedFrom":[subQ1,subQ0]});Q66=makeQuery(id+"F0.imprint","IMPRINT",FACE,{"disambiguationData":[TD([[makeQuery(id+"F0.imprint","IMPRINT",EDGE,{"disambiguationData":[TD([[subQ2,-1.0]])],"derivedFrom":subQ1}),1.0]])]});}
            var Q67;
            {var subQ0=sQuery(id+"F0.wireOp",EDGE,"E27");var subQ1=sQuery(id+"F0.wireOp",EDGE,"E4");var subQ2=makeQuery(id+"F0.imprint","INTERSECT",VERTEX,{"derivedFrom":[subQ1,subQ0]});Q67=makeQuery(id+"F0.imprint","IMPRINT",FACE,{"disambiguationData":[TD([[makeQuery(id+"F0.imprint","IMPRINT",EDGE,{"disambiguationData":[TD([[subQ2,-1.0]])],"derivedFrom":subQ1}),1.0]])]});}
            var Q68;
            {var subQ0=sQuery(id+"F0.wireOp",EDGE,"E24");var subQ1=sQuery(id+"F0.wireOp",EDGE,"E5");var subQ2=makeQuery(id+"F0.imprint","INTERSECT",VERTEX,{"derivedFrom":[subQ1,subQ0]});Q68=makeQuery(id+"F0.imprint","IMPRINT",FACE,{"disambiguationData":[TD([[makeQuery(id+"F0.imprint","IMPRINT",EDGE,{"disambiguationData":[TD([[subQ2,-1.0]])],"derivedFrom":subQ1}),1.0]])]});}
            var Q69;
            {var subQ0=sQuery(id+"F0.wireOp",EDGE,"E25");var subQ1=sQuery(id+"F0.wireOp",EDGE,"E18");var subQ2=makeQuery(id+"F0.imprint","INTERSECT",VERTEX,{"derivedFrom":[subQ1,subQ0]});Q69=makeQuery(id+"F0.imprint","IMPRINT",FACE,{"disambiguationData":[TD([[makeQuery(id+"F0.imprint","IMPRINT",EDGE,{"disambiguationData":[TD([[subQ2,-1.0]])],"derivedFrom":subQ1}),-1.0]])]});}
            var Q70;
            {var subQ0=sQuery(id+"F0.wireOp",EDGE,"E31");var subQ1=sQuery(id+"F0.wireOp",EDGE,"E17");var subQ2=makeQuery(id+"F0.imprint","INTERSECT",VERTEX,{"derivedFrom":[subQ1,subQ0]});Q70=makeQuery(id+"F0.imprint","IMPRINT",FACE,{"disambiguationData":[TD([[makeQuery(id+"F0.imprint","IMPRINT",EDGE,{"disambiguationData":[TD([[subQ2,-1.0]])],"derivedFrom":subQ1}),-1.0]])]});}
            var Q71;
            {var subQ0=sQuery(id+"F0.wireOp",EDGE,"E28");var subQ1=sQuery(id+"F0.wireOp",EDGE,"E19");var subQ2=makeQuery(id+"F0.imprint","INTERSECT",VERTEX,{"derivedFrom":[subQ1,subQ0]});Q71=makeQuery(id+"F0.imprint","IMPRINT",FACE,{"disambiguationData":[TD([[makeQuery(id+"F0.imprint","IMPRINT",EDGE,{"disambiguationData":[TD([[subQ2,-1.0]])],"derivedFrom":subQ1}),-1.0]])]});}
            var Q72;
            {var subQ0=sQuery(id+"F0.wireOp",EDGE,"E37");var subQ1=sQuery(id+"F0.wireOp",EDGE,"E5");var subQ2=makeQuery(id+"F0.imprint","INTERSECT",VERTEX,{"derivedFrom":[subQ1,subQ0]});Q72=makeQuery(id+"F0.imprint","IMPRINT",FACE,{"disambiguationData":[TD([[makeQuery(id+"F0.imprint","IMPRINT",EDGE,{"disambiguationData":[TD([[subQ2,-1.0]])],"derivedFrom":subQ1}),1.0]])]});}
            var Q73;
            {var subQ0=sQuery(id+"F0.wireOp",EDGE,"E32");var subQ1=sQuery(id+"F0.wireOp",EDGE,"E7");var subQ2=makeQuery(id+"F0.imprint","INTERSECT",VERTEX,{"derivedFrom":[subQ1,subQ0]});Q73=makeQuery(id+"F0.imprint","IMPRINT",FACE,{"disambiguationData":[TD([[makeQuery(id+"F0.imprint","IMPRINT",EDGE,{"disambiguationData":[TD([[subQ2,-1.0]])],"derivedFrom":subQ1}),1.0]])]});}
            var Q74;
            {var subQ0=sQuery(id+"F0.wireOp",EDGE,"E41");var subQ1=sQuery(id+"F0.wireOp",EDGE,"E0.left");var subQ2=makeQuery(id+"F0.imprint","INTERSECT",VERTEX,{"derivedFrom":[subQ1,subQ0]});Q74=makeQuery(id+"F0.imprint","IMPRINT",FACE,{"disambiguationData":[TD([[makeQuery(id+"F0.imprint","IMPRINT",EDGE,{"disambiguationData":[TD([[subQ2,1.0]])],"derivedFrom":subQ1}),-1.0]])]});}
            var Q75;
            {var subQ0=sQuery(id+"F0.wireOp",EDGE,"E33");var subQ1=sQuery(id+"F0.wireOp",EDGE,"E8");var subQ2=makeQuery(id+"F0.imprint","INTERSECT",VERTEX,{"derivedFrom":[subQ1,subQ0]});Q75=makeQuery(id+"F0.imprint","IMPRINT",FACE,{"disambiguationData":[TD([[makeQuery(id+"F0.imprint","IMPRINT",EDGE,{"disambiguationData":[TD([[subQ2,-1.0]])],"derivedFrom":subQ1}),1.0]])]});}
            var Q76;
            {var subQ0=sQuery(id+"F0.wireOp",EDGE,"E27");var subQ1=sQuery(id+"F0.wireOp",EDGE,"E3");var subQ2=makeQuery(id+"F0.imprint","INTERSECT",VERTEX,{"derivedFrom":[subQ1,subQ0]});Q76=makeQuery(id+"F0.imprint","IMPRINT",FACE,{"disambiguationData":[TD([[makeQuery(id+"F0.imprint","IMPRINT",EDGE,{"disambiguationData":[TD([[subQ2,-1.0]])],"derivedFrom":subQ1}),1.0]])]});}
            var Q77;
            {var subQ0=sQuery(id+"F0.wireOp",EDGE,"E40");var subQ1=sQuery(id+"F0.wireOp",EDGE,"E5");var subQ2=makeQuery(id+"F0.imprint","INTERSECT",VERTEX,{"derivedFrom":[subQ1,subQ0]});Q77=makeQuery(id+"F0.imprint","IMPRINT",FACE,{"disambiguationData":[TD([[makeQuery(id+"F0.imprint","IMPRINT",EDGE,{"disambiguationData":[TD([[subQ2,-1.0]])],"derivedFrom":subQ1}),1.0]])]});}
            var Q78;
            {var subQ1=sQuery(id+"F0.wireOp",EDGE,"E7");var subQ5=sQuery(id+"F0.wireOp",EDGE,"E36");var subQ6=makeQuery(id+"F0.imprint","INTERSECT",VERTEX,{"derivedFrom":[subQ1,subQ5]});Q78=makeQuery(id+"F0.imprint","IMPRINT",FACE,{"disambiguationData":[TD([[makeQuery(id+"F0.imprint","IMPRINT",EDGE,{"disambiguationData":[TD([[subQ6,-1.0]])],"derivedFrom":subQ1}),1.0]])]});}
            var Q79;
            {var subQ0=sQuery(id+"F0.wireOp",EDGE,"E29");var subQ1=sQuery(id+"F0.wireOp",EDGE,"E0.right");var subQ2=makeQuery(id+"F0.imprint","INTERSECT",VERTEX,{"derivedFrom":[subQ1,subQ0]});Q79=makeQuery(id+"F0.imprint","IMPRINT",FACE,{"disambiguationData":[TD([[makeQuery(id+"F0.imprint","IMPRINT",EDGE,{"disambiguationData":[TD([[subQ2,-1.0]])],"derivedFrom":subQ1}),1.0]])]});}
            var Q80;
            {var subQ0=sQuery(id+"F0.wireOp",EDGE,"E33");var subQ1=sQuery(id+"F0.wireOp",EDGE,"E1");var subQ2=makeQuery(id+"F0.imprint","INTERSECT",VERTEX,{"derivedFrom":[subQ1,subQ0]});Q80=makeQuery(id+"F0.imprint","IMPRINT",FACE,{"disambiguationData":[TD([[makeQuery(id+"F0.imprint","IMPRINT",EDGE,{"disambiguationData":[TD([[subQ2,-1.0]])],"derivedFrom":subQ1}),1.0]])]});}
            var Q81;
            {var subQ0=sQuery(id+"F0.wireOp",EDGE,"E31");var subQ1=sQuery(id+"F0.wireOp",EDGE,"E5");var subQ2=makeQuery(id+"F0.imprint","INTERSECT",VERTEX,{"derivedFrom":[subQ1,subQ0]});Q81=makeQuery(id+"F0.imprint","IMPRINT",FACE,{"disambiguationData":[TD([[makeQuery(id+"F0.imprint","IMPRINT",EDGE,{"disambiguationData":[TD([[subQ2,-1.0]])],"derivedFrom":subQ1}),1.0]])]});}
            var Q82;
            {var subQ0=sQuery(id+"F0.wireOp",EDGE,"E40");var subQ1=sQuery(id+"F0.wireOp",EDGE,"E1");var subQ2=makeQuery(id+"F0.imprint","INTERSECT",VERTEX,{"derivedFrom":[subQ1,subQ0]});Q82=makeQuery(id+"F0.imprint","IMPRINT",FACE,{"disambiguationData":[TD([[makeQuery(id+"F0.imprint","IMPRINT",EDGE,{"disambiguationData":[TD([[subQ2,-1.0]])],"derivedFrom":subQ1}),-1.0]])]});}
            var Q83;
            {var subQ0=sQuery(id+"F0.wireOp",EDGE,"E23");var subQ1=sQuery(id+"F0.wireOp",EDGE,"E0.left");var subQ2=makeQuery(id+"F0.imprint","INTERSECT",VERTEX,{"derivedFrom":[subQ1,subQ0]});Q83=makeQuery(id+"F0.imprint","IMPRINT",FACE,{"disambiguationData":[TD([[makeQuery(id+"F0.imprint","IMPRINT",EDGE,{"disambiguationData":[TD([[subQ2,-1.0]])],"derivedFrom":subQ1}),-1.0]])]});}
            var Q84;
            {var subQ0=sQuery(id+"F0.wireOp",EDGE,"E29");var subQ1=sQuery(id+"F0.wireOp",EDGE,"E1");var subQ2=makeQuery(id+"F0.imprint","INTERSECT",VERTEX,{"derivedFrom":[subQ1,subQ0]});Q84=makeQuery(id+"F0.imprint","IMPRINT",FACE,{"disambiguationData":[TD([[makeQuery(id+"F0.imprint","IMPRINT",EDGE,{"disambiguationData":[TD([[subQ2,-1.0]])],"derivedFrom":subQ1}),-1.0]])]});}
            var Q85;
            {var subQ0=sQuery(id+"F0.wireOp",EDGE,"E40");var subQ1=sQuery(id+"F0.wireOp",EDGE,"E3");var subQ2=makeQuery(id+"F0.imprint","INTERSECT",VERTEX,{"derivedFrom":[subQ1,subQ0]});Q85=makeQuery(id+"F0.imprint","IMPRINT",FACE,{"disambiguationData":[TD([[makeQuery(id+"F0.imprint","IMPRINT",EDGE,{"disambiguationData":[TD([[subQ2,-1.0]])],"derivedFrom":subQ1}),1.0]])]});}
            var Q86;
            {var subQ3=sQuery(id+"F0.wireOp",EDGE,"E19");var subQ7=sQuery(id+"F0.wireOp",EDGE,"E0.bottom");var subQ8=makeQuery(id+"F0.imprint","INTERSECT",VERTEX,{"derivedFrom":[subQ7,subQ3]});Q86=makeQuery(id+"F0.imprint","IMPRINT",FACE,{"disambiguationData":[TD([[makeQuery(id+"F0.imprint","IMPRINT",EDGE,{"disambiguationData":[TD([[subQ8,1.0]])],"derivedFrom":subQ7}),1.0]])]});}
            var Q87;
            {var subQ1=sQuery(id+"F0.wireOp",EDGE,"E0.left");var subQ3=sQuery(id+"F0.wireOp",EDGE,"E2");var subQ4=makeQuery(id+"F0.imprint","INTERSECT",VERTEX,{"derivedFrom":[subQ1,subQ3]});Q87=makeQuery(id+"F0.imprint","IMPRINT",FACE,{"disambiguationData":[TD([[makeQuery(id+"F0.imprint","IMPRINT",EDGE,{"disambiguationData":[TD([[subQ4,-1.0]])],"derivedFrom":subQ3}),-1.0]])]});}
            var Q88;
            {var subQ0=sQuery(id+"F0.wireOp",EDGE,"E17");var subQ1=sQuery(id+"F0.wireOp",EDGE,"E0.right");var subQ2=makeQuery(id+"F0.imprint","INTERSECT",VERTEX,{"derivedFrom":[subQ1,subQ0]});Q88=makeQuery(id+"F0.imprint","IMPRINT",FACE,{"disambiguationData":[TD([[makeQuery(id+"F0.imprint","IMPRINT",EDGE,{"disambiguationData":[TD([[subQ2,1.0]])],"derivedFrom":subQ1}),1.0]])]});}
            var Q89;
            {var subQ1=sQuery(id+"F0.wireOp",EDGE,"E0.right");var subQ3=sQuery(id+"F0.wireOp",EDGE,"E24");var subQ4=makeQuery(id+"F0.imprint","INTERSECT",VERTEX,{"derivedFrom":[subQ1,subQ3]});Q89=makeQuery(id+"F0.imprint","IMPRINT",FACE,{"disambiguationData":[TD([[makeQuery(id+"F0.imprint","IMPRINT",EDGE,{"disambiguationData":[TD([[subQ4,-1.0]])],"derivedFrom":subQ3}),1.0]])]});}
            var Q90;
            {var subQ0=sQuery(id+"F0.wireOp",EDGE,"E52");var subQ1=sQuery(id+"F0.wireOp",EDGE,"E1");var subQ2=makeQuery(id+"F0.imprint","INTERSECT",VERTEX,{"derivedFrom":[subQ1,subQ0]});Q90=makeQuery(id+"F0.imprint","IMPRINT",FACE,{"disambiguationData":[TD([[makeQuery(id+"F0.imprint","IMPRINT",EDGE,{"disambiguationData":[TD([[subQ2,-1.0]])],"derivedFrom":subQ1}),1.0]])]});}
            var Q91;
            {var subQ0=sQuery(id+"F0.wireOp",EDGE,"E30");var subQ1=sQuery(id+"F0.wireOp",EDGE,"E17");var subQ2=makeQuery(id+"F0.imprint","INTERSECT",VERTEX,{"derivedFrom":[subQ1,subQ0]});Q91=makeQuery(id+"F0.imprint","IMPRINT",FACE,{"disambiguationData":[TD([[makeQuery(id+"F0.imprint","IMPRINT",EDGE,{"disambiguationData":[TD([[subQ2,-1.0]])],"derivedFrom":subQ1}),-1.0]])]});}
            var Q92;
            {var subQ0=sQuery(id+"F0.wireOp",EDGE,"E40");var subQ1=sQuery(id+"F0.wireOp",EDGE,"E20");var subQ2=makeQuery(id+"F0.imprint","INTERSECT",VERTEX,{"derivedFrom":[subQ1,subQ0]});Q92=makeQuery(id+"F0.imprint","IMPRINT",FACE,{"disambiguationData":[TD([[makeQuery(id+"F0.imprint","IMPRINT",EDGE,{"disambiguationData":[TD([[subQ2,-1.0]])],"derivedFrom":subQ1}),-1.0]])]});}
            var Q93;
            {var subQ0=sQuery(id+"F0.wireOp",EDGE,"E44");var subQ1=sQuery(id+"F0.wireOp",EDGE,"E19");var subQ2=makeQuery(id+"F0.imprint","INTERSECT",VERTEX,{"derivedFrom":[subQ1,subQ0]});Q93=makeQuery(id+"F0.imprint","IMPRINT",FACE,{"disambiguationData":[TD([[makeQuery(id+"F0.imprint","IMPRINT",EDGE,{"disambiguationData":[TD([[subQ2,-1.0]])],"derivedFrom":subQ1}),-1.0]])]});}
            var Q94;
            {var subQ0=sQuery(id+"F0.wireOp",EDGE,"E43");var subQ1=sQuery(id+"F0.wireOp",EDGE,"E1");var subQ2=makeQuery(id+"F0.imprint","INTERSECT",VERTEX,{"derivedFrom":[subQ1,subQ0]});Q94=makeQuery(id+"F0.imprint","IMPRINT",FACE,{"disambiguationData":[TD([[makeQuery(id+"F0.imprint","IMPRINT",EDGE,{"disambiguationData":[TD([[subQ2,-1.0]])],"derivedFrom":subQ1}),1.0]])]});}
            var Q95;
            {var subQ0=sQuery(id+"F0.wireOp",EDGE,"E26");var subQ1=sQuery(id+"F0.wireOp",EDGE,"E1");var subQ2=makeQuery(id+"F0.imprint","INTERSECT",VERTEX,{"derivedFrom":[subQ1,subQ0]});Q95=makeQuery(id+"F0.imprint","IMPRINT",FACE,{"disambiguationData":[TD([[makeQuery(id+"F0.imprint","IMPRINT",EDGE,{"disambiguationData":[TD([[subQ2,-1.0]])],"derivedFrom":subQ1}),1.0]])]});}
            var Q96;
            {var subQ0=sQuery(id+"F0.wireOp",EDGE,"E44");var subQ1=sQuery(id+"F0.wireOp",EDGE,"E2");var subQ2=makeQuery(id+"F0.imprint","INTERSECT",VERTEX,{"derivedFrom":[subQ1,subQ0]});Q96=makeQuery(id+"F0.imprint","IMPRINT",FACE,{"disambiguationData":[TD([[makeQuery(id+"F0.imprint","IMPRINT",EDGE,{"disambiguationData":[TD([[subQ2,-1.0]])],"derivedFrom":subQ1}),1.0]])]});}
            var Q97;
            {var subQ0=sQuery(id+"F0.wireOp",EDGE,"E39");var subQ1=sQuery(id+"F0.wireOp",EDGE,"E0.left");var subQ2=makeQuery(id+"F0.imprint","INTERSECT",VERTEX,{"derivedFrom":[subQ1,subQ0]});Q97=makeQuery(id+"F0.imprint","IMPRINT",FACE,{"disambiguationData":[TD([[makeQuery(id+"F0.imprint","IMPRINT",EDGE,{"disambiguationData":[TD([[subQ2,1.0]])],"derivedFrom":subQ1}),-1.0]])]});}
            var Q98;
            {var subQ0=sQuery(id+"F0.wireOp",EDGE,"E31");var subQ1=sQuery(id+"F0.wireOp",EDGE,"E7");var subQ2=makeQuery(id+"F0.imprint","INTERSECT",VERTEX,{"derivedFrom":[subQ1,subQ0]});Q98=makeQuery(id+"F0.imprint","IMPRINT",FACE,{"disambiguationData":[TD([[makeQuery(id+"F0.imprint","IMPRINT",EDGE,{"disambiguationData":[TD([[subQ2,-1.0]])],"derivedFrom":subQ1}),1.0]])]});}
            var Q99;
            {var subQ0=sQuery(id+"F0.wireOp",EDGE,"E40");var subQ1=sQuery(id+"F0.wireOp",EDGE,"E19");var subQ2=makeQuery(id+"F0.imprint","INTERSECT",VERTEX,{"derivedFrom":[subQ1,subQ0]});Q99=makeQuery(id+"F0.imprint","IMPRINT",FACE,{"disambiguationData":[TD([[makeQuery(id+"F0.imprint","IMPRINT",EDGE,{"disambiguationData":[TD([[subQ2,-1.0]])],"derivedFrom":subQ1}),-1.0]])]});}
            var Q100;
            {var subQ0=sQuery(id+"F0.wireOp",EDGE,"E25");var subQ1=sQuery(id+"F0.wireOp",EDGE,"E20");var subQ2=makeQuery(id+"F0.imprint","INTERSECT",VERTEX,{"derivedFrom":[subQ1,subQ0]});Q100=makeQuery(id+"F0.imprint","IMPRINT",FACE,{"disambiguationData":[TD([[makeQuery(id+"F0.imprint","IMPRINT",EDGE,{"disambiguationData":[TD([[subQ2,-1.0]])],"derivedFrom":subQ1}),-1.0]])]});}
            var Q101;
            {var subQ0=sQuery(id+"F0.wireOp",EDGE,"E42");var subQ1=sQuery(id+"F0.wireOp",EDGE,"E0.bottom");var subQ2=makeQuery(id+"F0.imprint","INTERSECT",VERTEX,{"derivedFrom":[subQ1,subQ0]});Q101=makeQuery(id+"F0.imprint","IMPRINT",FACE,{"disambiguationData":[TD([[makeQuery(id+"F0.imprint","IMPRINT",EDGE,{"disambiguationData":[TD([[subQ2,-1.0]])],"derivedFrom":subQ1}),1.0]])]});}
            var Q102;
            {var subQ0=sQuery(id+"F0.wireOp",EDGE,"E43");var subQ1=sQuery(id+"F0.wireOp",EDGE,"E17");var subQ2=makeQuery(id+"F0.imprint","INTERSECT",VERTEX,{"derivedFrom":[subQ1,subQ0]});Q102=makeQuery(id+"F0.imprint","IMPRINT",FACE,{"disambiguationData":[TD([[makeQuery(id+"F0.imprint","IMPRINT",EDGE,{"disambiguationData":[TD([[subQ2,-1.0]])],"derivedFrom":subQ1}),-1.0]])]});}
            var Q103;
            {var subQ0=sQuery(id+"F0.wireOp",EDGE,"E29");var subQ1=sQuery(id+"F0.wireOp",EDGE,"E3");var subQ2=makeQuery(id+"F0.imprint","INTERSECT",VERTEX,{"derivedFrom":[subQ1,subQ0]});Q103=makeQuery(id+"F0.imprint","IMPRINT",FACE,{"disambiguationData":[TD([[makeQuery(id+"F0.imprint","IMPRINT",EDGE,{"disambiguationData":[TD([[subQ2,-1.0]])],"derivedFrom":subQ1}),1.0]])]});}
            var Q104;
            {var subQ0=sQuery(id+"F0.wireOp",EDGE,"E23");var subQ1=sQuery(id+"F0.wireOp",EDGE,"E5");var subQ2=makeQuery(id+"F0.imprint","INTERSECT",VERTEX,{"derivedFrom":[subQ1,subQ0]});Q104=makeQuery(id+"F0.imprint","IMPRINT",FACE,{"disambiguationData":[TD([[makeQuery(id+"F0.imprint","IMPRINT",EDGE,{"disambiguationData":[TD([[subQ2,-1.0]])],"derivedFrom":subQ1}),1.0]])]});}
            var Q105;
            {var subQ0=sQuery(id+"F0.wireOp",EDGE,"E31");var subQ1=sQuery(id+"F0.wireOp",EDGE,"E0.right");var subQ2=makeQuery(id+"F0.imprint","INTERSECT",VERTEX,{"derivedFrom":[subQ1,subQ0]});Q105=makeQuery(id+"F0.imprint","IMPRINT",FACE,{"disambiguationData":[TD([[makeQuery(id+"F0.imprint","IMPRINT",EDGE,{"disambiguationData":[TD([[subQ2,-1.0]])],"derivedFrom":subQ1}),1.0]])]});}
            var Q106;
            {var subQ0=sQuery(id+"F0.wireOp",EDGE,"E44");var subQ1=sQuery(id+"F0.wireOp",EDGE,"E1");var subQ2=makeQuery(id+"F0.imprint","INTERSECT",VERTEX,{"derivedFrom":[subQ1,subQ0]});Q106=makeQuery(id+"F0.imprint","IMPRINT",FACE,{"disambiguationData":[TD([[makeQuery(id+"F0.imprint","IMPRINT",EDGE,{"disambiguationData":[TD([[subQ2,-1.0]])],"derivedFrom":subQ1}),-1.0]])]});}
            var Q107;
            {var subQ0=sQuery(id+"F0.wireOp",EDGE,"E25");var subQ1=sQuery(id+"F0.wireOp",EDGE,"E1");var subQ2=makeQuery(id+"F0.imprint","INTERSECT",VERTEX,{"derivedFrom":[subQ1,subQ0]});Q107=makeQuery(id+"F0.imprint","IMPRINT",FACE,{"disambiguationData":[TD([[makeQuery(id+"F0.imprint","IMPRINT",EDGE,{"disambiguationData":[TD([[subQ2,-1.0]])],"derivedFrom":subQ1}),-1.0]])]});}
            var Q108;
            {var subQ0=sQuery(id+"F0.wireOp",EDGE,"E42");var subQ1=sQuery(id+"F0.wireOp",EDGE,"E19");var subQ2=makeQuery(id+"F0.imprint","INTERSECT",VERTEX,{"derivedFrom":[subQ1,subQ0]});Q108=makeQuery(id+"F0.imprint","IMPRINT",FACE,{"disambiguationData":[TD([[makeQuery(id+"F0.imprint","IMPRINT",EDGE,{"disambiguationData":[TD([[subQ2,-1.0]])],"derivedFrom":subQ1}),-1.0]])]});}
            var Q109;
            {var subQ0=sQuery(id+"F0.wireOp",EDGE,"E23");var subQ1=sQuery(id+"F0.wireOp",EDGE,"E4");var subQ2=makeQuery(id+"F0.imprint","INTERSECT",VERTEX,{"derivedFrom":[subQ1,subQ0]});Q109=makeQuery(id+"F0.imprint","IMPRINT",FACE,{"disambiguationData":[TD([[makeQuery(id+"F0.imprint","IMPRINT",EDGE,{"disambiguationData":[TD([[subQ2,-1.0]])],"derivedFrom":subQ1}),1.0]])]});}
            var Q110;
            {var subQ0=sQuery(id+"F0.wireOp",EDGE,"E41");var subQ1=sQuery(id+"F0.wireOp",EDGE,"E5");var subQ2=makeQuery(id+"F0.imprint","INTERSECT",VERTEX,{"derivedFrom":[subQ1,subQ0]});Q110=makeQuery(id+"F0.imprint","IMPRINT",FACE,{"disambiguationData":[TD([[makeQuery(id+"F0.imprint","IMPRINT",EDGE,{"disambiguationData":[TD([[subQ2,-1.0]])],"derivedFrom":subQ1}),1.0]])]});}
            var Q111;
            {var subQ0=sQuery(id+"F0.wireOp",EDGE,"E24");var subQ1=sQuery(id+"F0.wireOp",EDGE,"E1");var subQ2=makeQuery(id+"F0.imprint","INTERSECT",VERTEX,{"derivedFrom":[subQ1,subQ0]});Q111=makeQuery(id+"F0.imprint","IMPRINT",FACE,{"disambiguationData":[TD([[makeQuery(id+"F0.imprint","IMPRINT",EDGE,{"disambiguationData":[TD([[subQ2,-1.0]])],"derivedFrom":subQ1}),1.0]])]});}
            var Q112;
            {var subQ0=sQuery(id+"F0.wireOp",EDGE,"E36");var subQ1=sQuery(id+"F0.wireOp",EDGE,"E5");var subQ2=makeQuery(id+"F0.imprint","INTERSECT",VERTEX,{"derivedFrom":[subQ1,subQ0]});Q112=makeQuery(id+"F0.imprint","IMPRINT",FACE,{"disambiguationData":[TD([[makeQuery(id+"F0.imprint","IMPRINT",EDGE,{"disambiguationData":[TD([[subQ2,-1.0]])],"derivedFrom":subQ1}),1.0]])]});}
            var Q113;
            {var subQ0=sQuery(id+"F0.wireOp",EDGE,"E33");var subQ1=sQuery(id+"F0.wireOp",EDGE,"E6");var subQ2=makeQuery(id+"F0.imprint","INTERSECT",VERTEX,{"derivedFrom":[subQ1,subQ0]});Q113=makeQuery(id+"F0.imprint","IMPRINT",FACE,{"disambiguationData":[TD([[makeQuery(id+"F0.imprint","IMPRINT",EDGE,{"disambiguationData":[TD([[subQ2,-1.0]])],"derivedFrom":subQ1}),1.0]])]});}
            var Q114;
            {var subQ0=sQuery(id+"F0.wireOp",EDGE,"E32");var subQ1=sQuery(id+"F0.wireOp",EDGE,"E1");var subQ2=makeQuery(id+"F0.imprint","INTERSECT",VERTEX,{"derivedFrom":[subQ1,subQ0]});Q114=makeQuery(id+"F0.imprint","IMPRINT",FACE,{"disambiguationData":[TD([[makeQuery(id+"F0.imprint","IMPRINT",EDGE,{"disambiguationData":[TD([[subQ2,-1.0]])],"derivedFrom":subQ1}),1.0]])]});}
            var Q115;
            {var subQ0=sQuery(id+"F0.wireOp",EDGE,"E29");var subQ1=sQuery(id+"F0.wireOp",EDGE,"E2");var subQ2=makeQuery(id+"F0.imprint","INTERSECT",VERTEX,{"derivedFrom":[subQ1,subQ0]});Q115=makeQuery(id+"F0.imprint","IMPRINT",FACE,{"disambiguationData":[TD([[makeQuery(id+"F0.imprint","IMPRINT",EDGE,{"disambiguationData":[TD([[subQ2,-1.0]])],"derivedFrom":subQ1}),1.0]])]});}
            var Q116;
            {var subQ0=sQuery(id+"F0.wireOp",EDGE,"E40");var subQ1=sQuery(id+"F0.wireOp",EDGE,"E21");var subQ2=makeQuery(id+"F0.imprint","INTERSECT",VERTEX,{"derivedFrom":[subQ1,subQ0]});Q116=makeQuery(id+"F0.imprint","IMPRINT",FACE,{"disambiguationData":[TD([[makeQuery(id+"F0.imprint","IMPRINT",EDGE,{"disambiguationData":[TD([[subQ2,-1.0]])],"derivedFrom":subQ1}),-1.0]])]});}
            var Q117;
            {var subQ0=sQuery(id+"F0.wireOp",EDGE,"E26");var subQ1=sQuery(id+"F0.wireOp",EDGE,"E3");var subQ2=makeQuery(id+"F0.imprint","INTERSECT",VERTEX,{"derivedFrom":[subQ1,subQ0]});Q117=makeQuery(id+"F0.imprint","IMPRINT",FACE,{"disambiguationData":[TD([[makeQuery(id+"F0.imprint","IMPRINT",EDGE,{"disambiguationData":[TD([[subQ2,-1.0]])],"derivedFrom":subQ1}),1.0]])]});}
            var Q118;
            {var subQ0=sQuery(id+"F0.wireOp",EDGE,"E23");var subQ1=sQuery(id+"F0.wireOp",EDGE,"E20");var subQ2=makeQuery(id+"F0.imprint","INTERSECT",VERTEX,{"derivedFrom":[subQ1,subQ0]});Q118=makeQuery(id+"F0.imprint","IMPRINT",FACE,{"disambiguationData":[TD([[makeQuery(id+"F0.imprint","IMPRINT",EDGE,{"disambiguationData":[TD([[subQ2,-1.0]])],"derivedFrom":subQ1}),-1.0]])]});}
            var Q119;
            {var subQ0=sQuery(id+"F0.wireOp",EDGE,"E43");var subQ1=sQuery(id+"F0.wireOp",EDGE,"E0.left");var subQ2=makeQuery(id+"F0.imprint","INTERSECT",VERTEX,{"derivedFrom":[subQ1,subQ0]});Q119=makeQuery(id+"F0.imprint","IMPRINT",FACE,{"disambiguationData":[TD([[makeQuery(id+"F0.imprint","IMPRINT",EDGE,{"disambiguationData":[TD([[subQ2,1.0]])],"derivedFrom":subQ1}),-1.0]])]});}
            var Q120;
            {var subQ3=sQuery(id+"F0.wireOp",EDGE,"E21");var subQ6=sQuery(id+"F0.wireOp",EDGE,"E0.bottom");var subQ9=makeQuery(id+"F0.imprint","INTERSECT",VERTEX,{"derivedFrom":[subQ6,subQ3]});Q120=makeQuery(id+"F0.imprint","IMPRINT",FACE,{"disambiguationData":[TD([[makeQuery(id+"F0.imprint","IMPRINT",EDGE,{"disambiguationData":[TD([[subQ9,1.0]])],"derivedFrom":subQ6}),1.0]])]});}
            var Q121;
            {var subQ0=sQuery(id+"F0.wireOp",EDGE,"E21");var subQ1=sQuery(id+"F0.wireOp",EDGE,"E0.right");var subQ2=makeQuery(id+"F0.imprint","INTERSECT",VERTEX,{"derivedFrom":[subQ1,subQ0]});Q121=makeQuery(id+"F0.imprint","IMPRINT",FACE,{"disambiguationData":[TD([[makeQuery(id+"F0.imprint","IMPRINT",EDGE,{"disambiguationData":[TD([[subQ2,1.0]])],"derivedFrom":subQ1}),1.0]])]});}
            var Q122;
            {var subQ0=sQuery(id+"F0.wireOp",EDGE,"E49");var subQ1=sQuery(id+"F0.wireOp",EDGE,"E1");var subQ2=makeQuery(id+"F0.imprint","INTERSECT",VERTEX,{"derivedFrom":[subQ1,subQ0]});Q122=makeQuery(id+"F0.imprint","IMPRINT",FACE,{"disambiguationData":[TD([[makeQuery(id+"F0.imprint","IMPRINT",EDGE,{"disambiguationData":[TD([[subQ2,-1.0]])],"derivedFrom":subQ1}),1.0]])]});}
            var Q123;
            {var subQ0=sQuery(id+"F0.wireOp",EDGE,"E46");var subQ1=sQuery(id+"F0.wireOp",EDGE,"E23");var subQ2=makeQuery(id+"F0.imprint","INTERSECT",VERTEX,{"derivedFrom":[subQ1,subQ0]});Q123=makeQuery(id+"F0.imprint","IMPRINT",FACE,{"disambiguationData":[TD([[makeQuery(id+"F0.imprint","IMPRINT",EDGE,{"disambiguationData":[TD([[subQ2,-1.0]])],"derivedFrom":subQ1}),-1.0]])]});}
            var Q124;
            {var subQ1=sQuery(id+"F0.wireOp",EDGE,"E9");var subQ5=sQuery(id+"F0.wireOp",EDGE,"E34");var subQ6=makeQuery(id+"F0.imprint","INTERSECT",VERTEX,{"derivedFrom":[subQ1,subQ5]});Q124=makeQuery(id+"F0.imprint","IMPRINT",FACE,{"disambiguationData":[TD([[makeQuery(id+"F0.imprint","IMPRINT",EDGE,{"disambiguationData":[TD([[subQ6,-1.0]])],"derivedFrom":subQ1}),1.0]])]});}
            var Q125;
            {var subQ0=sQuery(id+"F0.wireOp",EDGE,"E23");var subQ1=sQuery(id+"F0.wireOp",EDGE,"E18");var subQ2=makeQuery(id+"F0.imprint","INTERSECT",VERTEX,{"derivedFrom":[subQ1,subQ0]});Q125=makeQuery(id+"F0.imprint","IMPRINT",FACE,{"disambiguationData":[TD([[makeQuery(id+"F0.imprint","IMPRINT",EDGE,{"disambiguationData":[TD([[subQ2,-1.0]])],"derivedFrom":subQ1}),-1.0]])]});}
            var Q126;
            {var subQ0=sQuery(id+"F0.wireOp",EDGE,"E26");var subQ1=sQuery(id+"F0.wireOp",EDGE,"E19");var subQ2=makeQuery(id+"F0.imprint","INTERSECT",VERTEX,{"derivedFrom":[subQ1,subQ0]});Q126=makeQuery(id+"F0.imprint","IMPRINT",FACE,{"disambiguationData":[TD([[makeQuery(id+"F0.imprint","IMPRINT",EDGE,{"disambiguationData":[TD([[subQ2,-1.0]])],"derivedFrom":subQ1}),-1.0]])]});}
            var Q127;
            {var subQ0=sQuery(id+"F0.wireOp",EDGE,"E23");var subQ1=sQuery(id+"F0.wireOp",EDGE,"E17");var subQ2=makeQuery(id+"F0.imprint","INTERSECT",VERTEX,{"derivedFrom":[subQ1,subQ0]});Q127=makeQuery(id+"F0.imprint","IMPRINT",FACE,{"disambiguationData":[TD([[makeQuery(id+"F0.imprint","IMPRINT",EDGE,{"disambiguationData":[TD([[subQ2,-1.0]])],"derivedFrom":subQ1}),-1.0]])]});}
            var Q128;
            {var subQ0=sQuery(id+"F0.wireOp",EDGE,"E24");var subQ1=sQuery(id+"F0.wireOp",EDGE,"E7");var subQ2=makeQuery(id+"F0.imprint","INTERSECT",VERTEX,{"derivedFrom":[subQ1,subQ0]});Q128=makeQuery(id+"F0.imprint","IMPRINT",FACE,{"disambiguationData":[TD([[makeQuery(id+"F0.imprint","IMPRINT",EDGE,{"disambiguationData":[TD([[subQ2,-1.0]])],"derivedFrom":subQ1}),1.0]])]});}
            var Q129;
            {var subQ0=sQuery(id+"F0.wireOp",EDGE,"E27");var subQ1=sQuery(id+"F0.wireOp",EDGE,"E21");var subQ2=makeQuery(id+"F0.imprint","INTERSECT",VERTEX,{"derivedFrom":[subQ1,subQ0]});Q129=makeQuery(id+"F0.imprint","IMPRINT",FACE,{"disambiguationData":[TD([[makeQuery(id+"F0.imprint","IMPRINT",EDGE,{"disambiguationData":[TD([[subQ2,-1.0]])],"derivedFrom":subQ1}),-1.0]])]});}
            var Q130;
            {var subQ1=sQuery(id+"F0.wireOp",EDGE,"E15");var subQ5=sQuery(id+"F0.wireOp",EDGE,"E28");var subQ6=makeQuery(id+"F0.imprint","INTERSECT",VERTEX,{"derivedFrom":[subQ1,subQ5]});Q130=makeQuery(id+"F0.imprint","IMPRINT",FACE,{"disambiguationData":[TD([[makeQuery(id+"F0.imprint","IMPRINT",EDGE,{"disambiguationData":[TD([[subQ6,-1.0]])],"derivedFrom":subQ1}),1.0]])]});}
            var Q131;
            {var subQ0=sQuery(id+"F0.wireOp",EDGE,"E35");var subQ1=sQuery(id+"F0.wireOp",EDGE,"E3");var subQ2=makeQuery(id+"F0.imprint","INTERSECT",VERTEX,{"derivedFrom":[subQ1,subQ0]});Q131=makeQuery(id+"F0.imprint","IMPRINT",FACE,{"disambiguationData":[TD([[makeQuery(id+"F0.imprint","IMPRINT",EDGE,{"disambiguationData":[TD([[subQ2,-1.0]])],"derivedFrom":subQ1}),1.0]])]});}
            var Q132;
            {var subQ3=sQuery(id+"F0.wireOp",EDGE,"E18");var subQ5=sQuery(id+"F0.wireOp",EDGE,"E0.bottom");var subQ6=makeQuery(id+"F0.imprint","INTERSECT",VERTEX,{"derivedFrom":[subQ5,subQ3]});Q132=makeQuery(id+"F0.imprint","IMPRINT",FACE,{"disambiguationData":[TD([[makeQuery(id+"F0.imprint","IMPRINT",EDGE,{"disambiguationData":[TD([[subQ6,1.0]])],"derivedFrom":subQ5}),1.0]])]});}
            var Q133;
            {var subQ0=sQuery(id+"F0.wireOp",EDGE,"E29");var subQ1=sQuery(id+"F0.wireOp",EDGE,"E18");var subQ2=makeQuery(id+"F0.imprint","INTERSECT",VERTEX,{"derivedFrom":[subQ1,subQ0]});Q133=makeQuery(id+"F0.imprint","IMPRINT",FACE,{"disambiguationData":[TD([[makeQuery(id+"F0.imprint","IMPRINT",EDGE,{"disambiguationData":[TD([[subQ2,-1.0]])],"derivedFrom":subQ1}),-1.0]])]});}
            var Q134;
            {var subQ0=sQuery(id+"F0.wireOp",EDGE,"E29");var subQ1=sQuery(id+"F0.wireOp",EDGE,"E5");var subQ2=makeQuery(id+"F0.imprint","INTERSECT",VERTEX,{"derivedFrom":[subQ1,subQ0]});Q134=makeQuery(id+"F0.imprint","IMPRINT",FACE,{"disambiguationData":[TD([[makeQuery(id+"F0.imprint","IMPRINT",EDGE,{"disambiguationData":[TD([[subQ2,-1.0]])],"derivedFrom":subQ1}),1.0]])]});}
            var Q135;
            {var subQ0=sQuery(id+"F0.wireOp",EDGE,"E29");var subQ1=sQuery(id+"F0.wireOp",EDGE,"E17");var subQ2=makeQuery(id+"F0.imprint","INTERSECT",VERTEX,{"derivedFrom":[subQ1,subQ0]});Q135=makeQuery(id+"F0.imprint","IMPRINT",FACE,{"disambiguationData":[TD([[makeQuery(id+"F0.imprint","IMPRINT",EDGE,{"disambiguationData":[TD([[subQ2,-1.0]])],"derivedFrom":subQ1}),-1.0]])]});}
            var Q136;
            {var subQ0=sQuery(id+"F0.wireOp",EDGE,"E31");var subQ1=sQuery(id+"F0.wireOp",EDGE,"E3");var subQ2=makeQuery(id+"F0.imprint","INTERSECT",VERTEX,{"derivedFrom":[subQ1,subQ0]});Q136=makeQuery(id+"F0.imprint","IMPRINT",FACE,{"disambiguationData":[TD([[makeQuery(id+"F0.imprint","IMPRINT",EDGE,{"disambiguationData":[TD([[subQ2,-1.0]])],"derivedFrom":subQ1}),1.0]])]});}
            var Q137;
            {var subQ0=sQuery(id+"F0.wireOp",EDGE,"E24");var subQ1=sQuery(id+"F0.wireOp",EDGE,"E19");var subQ2=makeQuery(id+"F0.imprint","INTERSECT",VERTEX,{"derivedFrom":[subQ1,subQ0]});Q137=makeQuery(id+"F0.imprint","IMPRINT",FACE,{"disambiguationData":[TD([[makeQuery(id+"F0.imprint","IMPRINT",EDGE,{"disambiguationData":[TD([[subQ2,-1.0]])],"derivedFrom":subQ1}),-1.0]])]});}
            var Q138;
            {var subQ0=sQuery(id+"F0.wireOp",EDGE,"E9");var subQ1=sQuery(id+"F0.wireOp",EDGE,"E0.left");var subQ2=makeQuery(id+"F0.imprint","INTERSECT",VERTEX,{"derivedFrom":[subQ1,subQ0]});Q138=makeQuery(id+"F0.imprint","IMPRINT",FACE,{"disambiguationData":[TD([[makeQuery(id+"F0.imprint","IMPRINT",EDGE,{"disambiguationData":[TD([[subQ2,-1.0]])],"derivedFrom":subQ1}),-1.0]])]});}
            var Q139;
            {var subQ0=sQuery(id+"F0.wireOp",EDGE,"E31");var subQ1=sQuery(id+"F0.wireOp",EDGE,"E8");var subQ2=makeQuery(id+"F0.imprint","INTERSECT",VERTEX,{"derivedFrom":[subQ1,subQ0]});Q139=makeQuery(id+"F0.imprint","IMPRINT",FACE,{"disambiguationData":[TD([[makeQuery(id+"F0.imprint","IMPRINT",EDGE,{"disambiguationData":[TD([[subQ2,-1.0]])],"derivedFrom":subQ1}),1.0]])]});}
            var Q140;
            {var subQ0=sQuery(id+"F0.wireOp",EDGE,"E41");var subQ1=sQuery(id+"F0.wireOp",EDGE,"E19");var subQ2=makeQuery(id+"F0.imprint","INTERSECT",VERTEX,{"derivedFrom":[subQ1,subQ0]});Q140=makeQuery(id+"F0.imprint","IMPRINT",FACE,{"disambiguationData":[TD([[makeQuery(id+"F0.imprint","IMPRINT",EDGE,{"disambiguationData":[TD([[subQ2,-1.0]])],"derivedFrom":subQ1}),-1.0]])]});}
            var Q141;
            {var subQ0=sQuery(id+"F0.wireOp",EDGE,"E30");var subQ1=sQuery(id+"F0.wireOp",EDGE,"E7");var subQ2=makeQuery(id+"F0.imprint","INTERSECT",VERTEX,{"derivedFrom":[subQ1,subQ0]});Q141=makeQuery(id+"F0.imprint","IMPRINT",FACE,{"disambiguationData":[TD([[makeQuery(id+"F0.imprint","IMPRINT",EDGE,{"disambiguationData":[TD([[subQ2,-1.0]])],"derivedFrom":subQ1}),1.0]])]});}
            var Q142;
            {var subQ0=sQuery(id+"F0.wireOp",EDGE,"E23");var subQ1=sQuery(id+"F0.wireOp",EDGE,"E22");var subQ2=makeQuery(id+"F0.imprint","INTERSECT",VERTEX,{"derivedFrom":[subQ1,subQ0]});Q142=makeQuery(id+"F0.imprint","IMPRINT",FACE,{"disambiguationData":[TD([[makeQuery(id+"F0.imprint","IMPRINT",EDGE,{"disambiguationData":[TD([[subQ2,-1.0]])],"derivedFrom":subQ1}),-1.0]])]});}
            var Q143;
            {var subQ3=sQuery(id+"F0.wireOp",EDGE,"E22");var subQ5=sQuery(id+"F0.wireOp",EDGE,"E0.bottom");var subQ6=makeQuery(id+"F0.imprint","INTERSECT",VERTEX,{"derivedFrom":[subQ5,subQ3]});Q143=makeQuery(id+"F0.imprint","IMPRINT",FACE,{"disambiguationData":[TD([[makeQuery(id+"F0.imprint","IMPRINT",EDGE,{"disambiguationData":[TD([[subQ6,1.0]])],"derivedFrom":subQ5}),1.0]])]});}
            var Q144;
            {var subQ0=sQuery(id+"F0.wireOp",EDGE,"E44");var subQ1=sQuery(id+"F0.wireOp",EDGE,"E17");var subQ2=makeQuery(id+"F0.imprint","INTERSECT",VERTEX,{"derivedFrom":[subQ1,subQ0]});Q144=makeQuery(id+"F0.imprint","IMPRINT",FACE,{"disambiguationData":[TD([[makeQuery(id+"F0.imprint","IMPRINT",EDGE,{"disambiguationData":[TD([[subQ2,-1.0]])],"derivedFrom":subQ1}),-1.0]])]});}
            var Q145;
            {var subQ0=sQuery(id+"F0.wireOp",EDGE,"E44");var subQ1=sQuery(id+"F0.wireOp",EDGE,"E18");var subQ2=makeQuery(id+"F0.imprint","INTERSECT",VERTEX,{"derivedFrom":[subQ1,subQ0]});Q145=makeQuery(id+"F0.imprint","IMPRINT",FACE,{"disambiguationData":[TD([[makeQuery(id+"F0.imprint","IMPRINT",EDGE,{"disambiguationData":[TD([[subQ2,-1.0]])],"derivedFrom":subQ1}),-1.0]])]});}
            var Q146;
            {var subQ0=sQuery(id+"F0.wireOp",EDGE,"E34");var subQ1=sQuery(id+"F0.wireOp",EDGE,"E7");var subQ2=makeQuery(id+"F0.imprint","INTERSECT",VERTEX,{"derivedFrom":[subQ1,subQ0]});Q146=makeQuery(id+"F0.imprint","IMPRINT",FACE,{"disambiguationData":[TD([[makeQuery(id+"F0.imprint","IMPRINT",EDGE,{"disambiguationData":[TD([[subQ2,-1.0]])],"derivedFrom":subQ1}),1.0]])]});}
            var Q147;
            {var subQ0=sQuery(id+"F0.wireOp",EDGE,"E40");var subQ1=sQuery(id+"F0.wireOp",EDGE,"E9");var subQ2=makeQuery(id+"F0.imprint","INTERSECT",VERTEX,{"derivedFrom":[subQ1,subQ0]});Q147=makeQuery(id+"F0.imprint","IMPRINT",FACE,{"disambiguationData":[TD([[makeQuery(id+"F0.imprint","IMPRINT",EDGE,{"disambiguationData":[TD([[subQ2,-1.0]])],"derivedFrom":subQ1}),1.0]])]});}
            var Q148;
            {var subQ0=sQuery(id+"F0.wireOp",EDGE,"E19");var subQ1=sQuery(id+"F0.wireOp",EDGE,"E0.right");var subQ2=makeQuery(id+"F0.imprint","INTERSECT",VERTEX,{"derivedFrom":[subQ1,subQ0]});Q148=makeQuery(id+"F0.imprint","IMPRINT",FACE,{"disambiguationData":[TD([[makeQuery(id+"F0.imprint","IMPRINT",EDGE,{"disambiguationData":[TD([[subQ2,1.0]])],"derivedFrom":subQ1}),1.0]])]});}
            var Q149;
            {var subQ0=sQuery(id+"F0.wireOp",EDGE,"E44");var subQ1=sQuery(id+"F0.wireOp",EDGE,"E1");var subQ2=makeQuery(id+"F0.imprint","INTERSECT",VERTEX,{"derivedFrom":[subQ1,subQ0]});Q149=makeQuery(id+"F0.imprint","IMPRINT",FACE,{"disambiguationData":[TD([[makeQuery(id+"F0.imprint","IMPRINT",EDGE,{"disambiguationData":[TD([[subQ2,-1.0]])],"derivedFrom":subQ1}),1.0]])]});}
            var Q150;
            {var subQ0=sQuery(id+"F0.wireOp",EDGE,"E25");var subQ1=sQuery(id+"F0.wireOp",EDGE,"E1");var subQ2=makeQuery(id+"F0.imprint","INTERSECT",VERTEX,{"derivedFrom":[subQ1,subQ0]});Q150=makeQuery(id+"F0.imprint","IMPRINT",FACE,{"disambiguationData":[TD([[makeQuery(id+"F0.imprint","IMPRINT",EDGE,{"disambiguationData":[TD([[subQ2,-1.0]])],"derivedFrom":subQ1}),1.0]])]});}
            var Q151;
            {var subQ0=sQuery(id+"F0.wireOp",EDGE,"E50");var subQ1=sQuery(id+"F0.wireOp",EDGE,"E2");var subQ2=makeQuery(id+"F0.imprint","INTERSECT",VERTEX,{"derivedFrom":[subQ1,subQ0]});Q151=makeQuery(id+"F0.imprint","IMPRINT",FACE,{"disambiguationData":[TD([[makeQuery(id+"F0.imprint","IMPRINT",EDGE,{"disambiguationData":[TD([[subQ2,-1.0]])],"derivedFrom":subQ1}),1.0]])]});}
            var Q152;
            {var subQ0=sQuery(id+"F0.wireOp",EDGE,"E33");var subQ1=sQuery(id+"F0.wireOp",EDGE,"E9");var subQ2=makeQuery(id+"F0.imprint","INTERSECT",VERTEX,{"derivedFrom":[subQ1,subQ0]});Q152=makeQuery(id+"F0.imprint","IMPRINT",FACE,{"disambiguationData":[TD([[makeQuery(id+"F0.imprint","IMPRINT",EDGE,{"disambiguationData":[TD([[subQ2,-1.0]])],"derivedFrom":subQ1}),1.0]])]});}
            var Q153;
            {var subQ0=sQuery(id+"F0.wireOp",EDGE,"E49");var subQ1=sQuery(id+"F0.wireOp",EDGE,"E17");var subQ2=makeQuery(id+"F0.imprint","INTERSECT",VERTEX,{"derivedFrom":[subQ1,subQ0]});Q153=makeQuery(id+"F0.imprint","IMPRINT",FACE,{"disambiguationData":[TD([[makeQuery(id+"F0.imprint","IMPRINT",EDGE,{"disambiguationData":[TD([[subQ2,-1.0]])],"derivedFrom":subQ1}),-1.0]])]});}
            var Q154;
            {var subQ0=sQuery(id+"F0.wireOp",EDGE,"E42");var subQ1=sQuery(id+"F0.wireOp",EDGE,"E5");var subQ2=makeQuery(id+"F0.imprint","INTERSECT",VERTEX,{"derivedFrom":[subQ1,subQ0]});Q154=makeQuery(id+"F0.imprint","IMPRINT",FACE,{"disambiguationData":[TD([[makeQuery(id+"F0.imprint","IMPRINT",EDGE,{"disambiguationData":[TD([[subQ2,-1.0]])],"derivedFrom":subQ1}),1.0]])]});}
            var Q155;
            {var subQ0=sQuery(id+"F0.wireOp",EDGE,"E35");var subQ1=sQuery(id+"F0.wireOp",EDGE,"E6");var subQ2=makeQuery(id+"F0.imprint","INTERSECT",VERTEX,{"derivedFrom":[subQ1,subQ0]});Q155=makeQuery(id+"F0.imprint","IMPRINT",FACE,{"disambiguationData":[TD([[makeQuery(id+"F0.imprint","IMPRINT",EDGE,{"disambiguationData":[TD([[subQ2,-1.0]])],"derivedFrom":subQ1}),1.0]])]});}
            var Q156;
            {var subQ0=sQuery(id+"F0.wireOp",EDGE,"E23");var subQ1=sQuery(id+"F0.wireOp",EDGE,"E1");var subQ2=makeQuery(id+"F0.imprint","INTERSECT",VERTEX,{"derivedFrom":[subQ1,subQ0]});Q156=makeQuery(id+"F0.imprint","IMPRINT",FACE,{"disambiguationData":[TD([[makeQuery(id+"F0.imprint","IMPRINT",EDGE,{"disambiguationData":[TD([[subQ2,-1.0]])],"derivedFrom":subQ1}),-1.0]])]});}
            var Q157;
            {var subQ0=sQuery(id+"F0.wireOp",EDGE,"E42");var subQ1=sQuery(id+"F0.wireOp",EDGE,"E21");var subQ2=makeQuery(id+"F0.imprint","INTERSECT",VERTEX,{"derivedFrom":[subQ1,subQ0]});Q157=makeQuery(id+"F0.imprint","IMPRINT",FACE,{"disambiguationData":[TD([[makeQuery(id+"F0.imprint","IMPRINT",EDGE,{"disambiguationData":[TD([[subQ2,-1.0]])],"derivedFrom":subQ1}),-1.0]])]});}
            var Q158;
            {var subQ0=sQuery(id+"F0.wireOp",EDGE,"E42");var subQ1=sQuery(id+"F0.wireOp",EDGE,"E6");var subQ2=makeQuery(id+"F0.imprint","INTERSECT",VERTEX,{"derivedFrom":[subQ1,subQ0]});Q158=makeQuery(id+"F0.imprint","IMPRINT",FACE,{"disambiguationData":[TD([[makeQuery(id+"F0.imprint","IMPRINT",EDGE,{"disambiguationData":[TD([[subQ2,-1.0]])],"derivedFrom":subQ1}),1.0]])]});}
            var Q159;
            {var subQ0=sQuery(id+"F0.wireOp",EDGE,"E31");var subQ1=sQuery(id+"F0.wireOp",EDGE,"E1");var subQ2=makeQuery(id+"F0.imprint","INTERSECT",VERTEX,{"derivedFrom":[subQ1,subQ0]});Q159=makeQuery(id+"F0.imprint","IMPRINT",FACE,{"disambiguationData":[TD([[makeQuery(id+"F0.imprint","IMPRINT",EDGE,{"disambiguationData":[TD([[subQ2,-1.0]])],"derivedFrom":subQ1}),-1.0]])]});}
            var Q160;
            {var subQ0=sQuery(id+"F0.wireOp",EDGE,"E42");var subQ1=sQuery(id+"F0.wireOp",EDGE,"E3");var subQ2=makeQuery(id+"F0.imprint","INTERSECT",VERTEX,{"derivedFrom":[subQ1,subQ0]});Q160=makeQuery(id+"F0.imprint","IMPRINT",FACE,{"disambiguationData":[TD([[makeQuery(id+"F0.imprint","IMPRINT",EDGE,{"disambiguationData":[TD([[subQ2,-1.0]])],"derivedFrom":subQ1}),1.0]])]});}
            var Q161;
            {var subQ0=sQuery(id+"F0.wireOp",EDGE,"E15");var subQ1=sQuery(id+"F0.wireOp",EDGE,"E0.left");var subQ2=makeQuery(id+"F0.imprint","INTERSECT",VERTEX,{"derivedFrom":[subQ1,subQ0]});Q161=makeQuery(id+"F0.imprint","IMPRINT",FACE,{"disambiguationData":[TD([[makeQuery(id+"F0.imprint","IMPRINT",EDGE,{"disambiguationData":[TD([[subQ2,-1.0]])],"derivedFrom":subQ1}),-1.0]])]});}
            var Q162;
            {var subQ0=sQuery(id+"F0.wireOp",EDGE,"E37");var subQ1=sQuery(id+"F0.wireOp",EDGE,"E0.right");var subQ2=makeQuery(id+"F0.imprint","INTERSECT",VERTEX,{"derivedFrom":[subQ1,subQ0]});Q162=makeQuery(id+"F0.imprint","IMPRINT",FACE,{"disambiguationData":[TD([[makeQuery(id+"F0.imprint","IMPRINT",EDGE,{"disambiguationData":[TD([[subQ2,-1.0]])],"derivedFrom":subQ1}),1.0]])]});}
            var Q163;
            {var subQ0=sQuery(id+"F0.wireOp",EDGE,"E41");var subQ1=sQuery(id+"F0.wireOp",EDGE,"E21");var subQ2=makeQuery(id+"F0.imprint","INTERSECT",VERTEX,{"derivedFrom":[subQ1,subQ0]});Q163=makeQuery(id+"F0.imprint","IMPRINT",FACE,{"disambiguationData":[TD([[makeQuery(id+"F0.imprint","IMPRINT",EDGE,{"disambiguationData":[TD([[subQ2,-1.0]])],"derivedFrom":subQ1}),-1.0]])]});}
            var Q164;
            {var subQ1=sQuery(id+"F0.wireOp",EDGE,"E8");var subQ5=sQuery(id+"F0.wireOp",EDGE,"E35");var subQ6=makeQuery(id+"F0.imprint","INTERSECT",VERTEX,{"derivedFrom":[subQ1,subQ5]});Q164=makeQuery(id+"F0.imprint","IMPRINT",FACE,{"disambiguationData":[TD([[makeQuery(id+"F0.imprint","IMPRINT",EDGE,{"disambiguationData":[TD([[subQ6,-1.0]])],"derivedFrom":subQ1}),1.0]])]});}
            var Q165;
            {var subQ0=sQuery(id+"F0.wireOp",EDGE,"E39");var subQ1=sQuery(id+"F0.wireOp",EDGE,"E17");var subQ2=makeQuery(id+"F0.imprint","INTERSECT",VERTEX,{"derivedFrom":[subQ1,subQ0]});Q165=makeQuery(id+"F0.imprint","IMPRINT",FACE,{"disambiguationData":[TD([[makeQuery(id+"F0.imprint","IMPRINT",EDGE,{"disambiguationData":[TD([[subQ2,-1.0]])],"derivedFrom":subQ1}),-1.0]])]});}
            var Q166;
            {var subQ0=sQuery(id+"F0.wireOp",EDGE,"E25");var subQ1=sQuery(id+"F0.wireOp",EDGE,"E19");var subQ2=makeQuery(id+"F0.imprint","INTERSECT",VERTEX,{"derivedFrom":[subQ1,subQ0]});Q166=makeQuery(id+"F0.imprint","IMPRINT",FACE,{"disambiguationData":[TD([[makeQuery(id+"F0.imprint","IMPRINT",EDGE,{"disambiguationData":[TD([[subQ2,-1.0]])],"derivedFrom":subQ1}),-1.0]])]});}
            var Q167;
            {var subQ0=sQuery(id+"F0.wireOp",EDGE,"E23");var subQ1=sQuery(id+"F0.wireOp",EDGE,"E7");var subQ2=makeQuery(id+"F0.imprint","INTERSECT",VERTEX,{"derivedFrom":[subQ1,subQ0]});Q167=makeQuery(id+"F0.imprint","IMPRINT",FACE,{"disambiguationData":[TD([[makeQuery(id+"F0.imprint","IMPRINT",EDGE,{"disambiguationData":[TD([[subQ2,-1.0]])],"derivedFrom":subQ1}),1.0]])]});}
            var Q168;
            {var subQ0=sQuery(id+"F0.wireOp",EDGE,"E31");var subQ1=sQuery(id+"F0.wireOp",EDGE,"E10");var subQ2=makeQuery(id+"F0.imprint","INTERSECT",VERTEX,{"derivedFrom":[subQ1,subQ0]});Q168=makeQuery(id+"F0.imprint","IMPRINT",FACE,{"disambiguationData":[TD([[makeQuery(id+"F0.imprint","IMPRINT",EDGE,{"disambiguationData":[TD([[subQ2,-1.0]])],"derivedFrom":subQ1}),1.0]])]});}
            var Q169;
            {var subQ0=sQuery(id+"F0.wireOp",EDGE,"E34");var subQ1=sQuery(id+"F0.wireOp",EDGE,"E3");var subQ2=makeQuery(id+"F0.imprint","INTERSECT",VERTEX,{"derivedFrom":[subQ1,subQ0]});Q169=makeQuery(id+"F0.imprint","IMPRINT",FACE,{"disambiguationData":[TD([[makeQuery(id+"F0.imprint","IMPRINT",EDGE,{"disambiguationData":[TD([[subQ2,-1.0]])],"derivedFrom":subQ1}),1.0]])]});}
            var Q170;
            {var subQ0=sQuery(id+"F0.wireOp",EDGE,"E28");var subQ1=sQuery(id+"F0.wireOp",EDGE,"E5");var subQ2=makeQuery(id+"F0.imprint","INTERSECT",VERTEX,{"derivedFrom":[subQ1,subQ0]});Q170=makeQuery(id+"F0.imprint","IMPRINT",FACE,{"disambiguationData":[TD([[makeQuery(id+"F0.imprint","IMPRINT",EDGE,{"disambiguationData":[TD([[subQ2,-1.0]])],"derivedFrom":subQ1}),1.0]])]});}
            var Q171;
            {var subQ0=sQuery(id+"F0.wireOp",EDGE,"E31");var subQ1=sQuery(id+"F0.wireOp",EDGE,"E4");var subQ2=makeQuery(id+"F0.imprint","INTERSECT",VERTEX,{"derivedFrom":[subQ1,subQ0]});Q171=makeQuery(id+"F0.imprint","IMPRINT",FACE,{"disambiguationData":[TD([[makeQuery(id+"F0.imprint","IMPRINT",EDGE,{"disambiguationData":[TD([[subQ2,-1.0]])],"derivedFrom":subQ1}),1.0]])]});}
            var Q172;
            {var subQ0=sQuery(id+"F0.wireOp",EDGE,"E25");var subQ1=sQuery(id+"F0.wireOp",EDGE,"E6");var subQ2=makeQuery(id+"F0.imprint","INTERSECT",VERTEX,{"derivedFrom":[subQ1,subQ0]});Q172=makeQuery(id+"F0.imprint","IMPRINT",FACE,{"disambiguationData":[TD([[makeQuery(id+"F0.imprint","IMPRINT",EDGE,{"disambiguationData":[TD([[subQ2,-1.0]])],"derivedFrom":subQ1}),1.0]])]});}
            var Q173;
            {var subQ0=sQuery(id+"F0.wireOp",EDGE,"E41");var subQ1=sQuery(id+"F0.wireOp",EDGE,"E1");var subQ2=makeQuery(id+"F0.imprint","INTERSECT",VERTEX,{"derivedFrom":[subQ1,subQ0]});Q173=makeQuery(id+"F0.imprint","IMPRINT",FACE,{"disambiguationData":[TD([[makeQuery(id+"F0.imprint","IMPRINT",EDGE,{"disambiguationData":[TD([[subQ2,-1.0]])],"derivedFrom":subQ1}),1.0]])]});}
            var Q174;
            {var subQ0=sQuery(id+"F0.wireOp",EDGE,"E28");var subQ1=sQuery(id+"F0.wireOp",EDGE,"E1");var subQ2=makeQuery(id+"F0.imprint","INTERSECT",VERTEX,{"derivedFrom":[subQ1,subQ0]});Q174=makeQuery(id+"F0.imprint","IMPRINT",FACE,{"disambiguationData":[TD([[makeQuery(id+"F0.imprint","IMPRINT",EDGE,{"disambiguationData":[TD([[subQ2,-1.0]])],"derivedFrom":subQ1}),1.0]])]});}
            var Q175;
            {var subQ0=sQuery(id+"F0.wireOp",EDGE,"E40");var subQ1=sQuery(id+"F0.wireOp",EDGE,"E2");var subQ2=makeQuery(id+"F0.imprint","INTERSECT",VERTEX,{"derivedFrom":[subQ1,subQ0]});Q175=makeQuery(id+"F0.imprint","IMPRINT",FACE,{"disambiguationData":[TD([[makeQuery(id+"F0.imprint","IMPRINT",EDGE,{"disambiguationData":[TD([[subQ2,-1.0]])],"derivedFrom":subQ1}),1.0]])]});}
            var Q176;
            {var subQ0=sQuery(id+"F0.wireOp",EDGE,"E40");var subQ1=sQuery(id+"F0.wireOp",EDGE,"E8");var subQ2=makeQuery(id+"F0.imprint","INTERSECT",VERTEX,{"derivedFrom":[subQ1,subQ0]});Q176=makeQuery(id+"F0.imprint","IMPRINT",FACE,{"disambiguationData":[TD([[makeQuery(id+"F0.imprint","IMPRINT",EDGE,{"disambiguationData":[TD([[subQ2,-1.0]])],"derivedFrom":subQ1}),1.0]])]});}
            var Q177;
            {var subQ0=sQuery(id+"F0.wireOp",EDGE,"E43");var subQ1=sQuery(id+"F0.wireOp",EDGE,"E3");var subQ2=makeQuery(id+"F0.imprint","INTERSECT",VERTEX,{"derivedFrom":[subQ1,subQ0]});Q177=makeQuery(id+"F0.imprint","IMPRINT",FACE,{"disambiguationData":[TD([[makeQuery(id+"F0.imprint","IMPRINT",EDGE,{"disambiguationData":[TD([[subQ2,-1.0]])],"derivedFrom":subQ1}),1.0]])]});}
            var Q178;
            {var subQ0=sQuery(id+"F0.wireOp",EDGE,"E25");var subQ1=sQuery(id+"F0.wireOp",EDGE,"E0.left");var subQ2=makeQuery(id+"F0.imprint","INTERSECT",VERTEX,{"derivedFrom":[subQ1,subQ0]});Q178=makeQuery(id+"F0.imprint","IMPRINT",FACE,{"disambiguationData":[TD([[makeQuery(id+"F0.imprint","IMPRINT",EDGE,{"disambiguationData":[TD([[subQ2,-1.0]])],"derivedFrom":subQ1}),-1.0]])]});}
            var Q179;
            {var subQ0=sQuery(id+"F0.wireOp",EDGE,"E3");var subQ1=sQuery(id+"F0.wireOp",EDGE,"E0.right");var subQ2=makeQuery(id+"F0.imprint","INTERSECT",VERTEX,{"derivedFrom":[subQ1,subQ0]});Q179=makeQuery(id+"F0.imprint","IMPRINT",FACE,{"disambiguationData":[TD([[makeQuery(id+"F0.imprint","IMPRINT",EDGE,{"disambiguationData":[TD([[subQ2,-1.0]])],"derivedFrom":subQ1}),1.0]])]});}
            var Q180;
            {var subQ0=sQuery(id+"F0.wireOp",EDGE,"E33");var subQ1=sQuery(id+"F0.wireOp",EDGE,"E7");var subQ2=makeQuery(id+"F0.imprint","INTERSECT",VERTEX,{"derivedFrom":[subQ1,subQ0]});Q180=makeQuery(id+"F0.imprint","IMPRINT",FACE,{"disambiguationData":[TD([[makeQuery(id+"F0.imprint","IMPRINT",EDGE,{"disambiguationData":[TD([[subQ2,-1.0]])],"derivedFrom":subQ1}),1.0]])]});}
            var Q181;
            {var subQ0=sQuery(id+"F0.wireOp",EDGE,"E25");var subQ1=sQuery(id+"F0.wireOp",EDGE,"E3");var subQ2=makeQuery(id+"F0.imprint","INTERSECT",VERTEX,{"derivedFrom":[subQ1,subQ0]});Q181=makeQuery(id+"F0.imprint","IMPRINT",FACE,{"disambiguationData":[TD([[makeQuery(id+"F0.imprint","IMPRINT",EDGE,{"disambiguationData":[TD([[subQ2,-1.0]])],"derivedFrom":subQ1}),1.0]])]});}
            var Q182;
            {var subQ0=sQuery(id+"F0.wireOp",EDGE,"E31");var subQ1=sQuery(id+"F0.wireOp",EDGE,"E2");var subQ2=makeQuery(id+"F0.imprint","INTERSECT",VERTEX,{"derivedFrom":[subQ1,subQ0]});Q182=makeQuery(id+"F0.imprint","IMPRINT",FACE,{"disambiguationData":[TD([[makeQuery(id+"F0.imprint","IMPRINT",EDGE,{"disambiguationData":[TD([[subQ2,-1.0]])],"derivedFrom":subQ1}),1.0]])]});}
            var Q183;
            {var subQ0=sQuery(id+"F0.wireOp",EDGE,"E28");var subQ1=sQuery(id+"F0.wireOp",EDGE,"E3");var subQ2=makeQuery(id+"F0.imprint","INTERSECT",VERTEX,{"derivedFrom":[subQ1,subQ0]});Q183=makeQuery(id+"F0.imprint","IMPRINT",FACE,{"disambiguationData":[TD([[makeQuery(id+"F0.imprint","IMPRINT",EDGE,{"disambiguationData":[TD([[subQ2,-1.0]])],"derivedFrom":subQ1}),1.0]])]});}
            var Q184;
            {var subQ0=sQuery(id+"F0.wireOp",EDGE,"E5");var subQ1=sQuery(id+"F0.wireOp",EDGE,"E0.left");var subQ2=makeQuery(id+"F0.imprint","INTERSECT",VERTEX,{"derivedFrom":[subQ1,subQ0]});Q184=makeQuery(id+"F0.imprint","IMPRINT",FACE,{"disambiguationData":[TD([[makeQuery(id+"F0.imprint","IMPRINT",EDGE,{"disambiguationData":[TD([[subQ2,-1.0]])],"derivedFrom":subQ1}),-1.0]])]});}
            var Q185;
            {var subQ0=sQuery(id+"F0.wireOp",EDGE,"E25");var subQ1=sQuery(id+"F0.wireOp",EDGE,"E22");var subQ2=makeQuery(id+"F0.imprint","INTERSECT",VERTEX,{"derivedFrom":[subQ1,subQ0]});Q185=makeQuery(id+"F0.imprint","IMPRINT",FACE,{"disambiguationData":[TD([[makeQuery(id+"F0.imprint","IMPRINT",EDGE,{"disambiguationData":[TD([[subQ2,-1.0]])],"derivedFrom":subQ1}),-1.0]])]});}
            var Q186;
            {var subQ0=sQuery(id+"F0.wireOp",EDGE,"E33");var subQ1=sQuery(id+"F0.wireOp",EDGE,"E4");var subQ2=makeQuery(id+"F0.imprint","INTERSECT",VERTEX,{"derivedFrom":[subQ1,subQ0]});Q186=makeQuery(id+"F0.imprint","IMPRINT",FACE,{"disambiguationData":[TD([[makeQuery(id+"F0.imprint","IMPRINT",EDGE,{"disambiguationData":[TD([[subQ2,-1.0]])],"derivedFrom":subQ1}),1.0]])]});}
            var Q187;
            {var subQ0=sQuery(id+"F0.wireOp",EDGE,"E27");var subQ1=sQuery(id+"F0.wireOp",EDGE,"E6");var subQ2=makeQuery(id+"F0.imprint","INTERSECT",VERTEX,{"derivedFrom":[subQ1,subQ0]});Q187=makeQuery(id+"F0.imprint","IMPRINT",FACE,{"disambiguationData":[TD([[makeQuery(id+"F0.imprint","IMPRINT",EDGE,{"disambiguationData":[TD([[subQ2,-1.0]])],"derivedFrom":subQ1}),1.0]])]});}
            var Q188;
            {var subQ0=sQuery(id+"F0.wireOp",EDGE,"E30");var subQ1=sQuery(id+"F0.wireOp",EDGE,"E5");var subQ2=makeQuery(id+"F0.imprint","INTERSECT",VERTEX,{"derivedFrom":[subQ1,subQ0]});Q188=makeQuery(id+"F0.imprint","IMPRINT",FACE,{"disambiguationData":[TD([[makeQuery(id+"F0.imprint","IMPRINT",EDGE,{"disambiguationData":[TD([[subQ2,-1.0]])],"derivedFrom":subQ1}),1.0]])]});}
            var Q189;
            {var subQ0=sQuery(id+"F0.wireOp",EDGE,"E29");var subQ1=sQuery(id+"F0.wireOp",EDGE,"E1");var subQ2=makeQuery(id+"F0.imprint","INTERSECT",VERTEX,{"derivedFrom":[subQ1,subQ0]});Q189=makeQuery(id+"F0.imprint","IMPRINT",FACE,{"disambiguationData":[TD([[makeQuery(id+"F0.imprint","IMPRINT",EDGE,{"disambiguationData":[TD([[subQ2,-1.0]])],"derivedFrom":subQ1}),1.0]])]});}
            var Q190;
            {var subQ0=sQuery(id+"F0.wireOp",EDGE,"E23");var subQ1=sQuery(id+"F0.wireOp",EDGE,"E2");var subQ2=makeQuery(id+"F0.imprint","INTERSECT",VERTEX,{"derivedFrom":[subQ1,subQ0]});Q190=makeQuery(id+"F0.imprint","IMPRINT",FACE,{"disambiguationData":[TD([[makeQuery(id+"F0.imprint","IMPRINT",EDGE,{"disambiguationData":[TD([[subQ2,-1.0]])],"derivedFrom":subQ1}),1.0]])]});}
            var Q191;
            {var subQ0=sQuery(id+"F0.wireOp",EDGE,"E41");var subQ1=sQuery(id+"F0.wireOp",EDGE,"E3");var subQ2=makeQuery(id+"F0.imprint","INTERSECT",VERTEX,{"derivedFrom":[subQ1,subQ0]});Q191=makeQuery(id+"F0.imprint","IMPRINT",FACE,{"disambiguationData":[TD([[makeQuery(id+"F0.imprint","IMPRINT",EDGE,{"disambiguationData":[TD([[subQ2,-1.0]])],"derivedFrom":subQ1}),1.0]])]});}
            var Q192;
            {var subQ0=sQuery(id+"F0.wireOp",EDGE,"E44");var subQ1=sQuery(id+"F0.wireOp",EDGE,"E4");var subQ2=makeQuery(id+"F0.imprint","INTERSECT",VERTEX,{"derivedFrom":[subQ1,subQ0]});Q192=makeQuery(id+"F0.imprint","IMPRINT",FACE,{"disambiguationData":[TD([[makeQuery(id+"F0.imprint","IMPRINT",EDGE,{"disambiguationData":[TD([[subQ2,-1.0]])],"derivedFrom":subQ1}),1.0]])]});}
            var Q193;
            {var subQ0=sQuery(id+"F0.wireOp",EDGE,"E41");var subQ1=sQuery(id+"F0.wireOp",EDGE,"E7");var subQ2=makeQuery(id+"F0.imprint","INTERSECT",VERTEX,{"derivedFrom":[subQ1,subQ0]});Q193=makeQuery(id+"F0.imprint","IMPRINT",FACE,{"disambiguationData":[TD([[makeQuery(id+"F0.imprint","IMPRINT",EDGE,{"disambiguationData":[TD([[subQ2,-1.0]])],"derivedFrom":subQ1}),1.0]])]});}
            var Q194;
            {var subQ3=sQuery(id+"F0.wireOp",EDGE,"E27");var subQ5=sQuery(id+"F0.wireOp",EDGE,"E16");var subQ7=makeQuery(id+"F0.imprint","INTERSECT",VERTEX,{"derivedFrom":[subQ5,subQ3]});Q194=makeQuery(id+"F0.imprint","IMPRINT",FACE,{"disambiguationData":[TD([[makeQuery(id+"F0.imprint","IMPRINT",EDGE,{"disambiguationData":[TD([[subQ7,-1.0]])],"derivedFrom":subQ5}),1.0]])]});}
            var Q195;
            {var subQ1=sQuery(id+"F0.wireOp",EDGE,"E0.right");var subQ3=sQuery(id+"F0.wireOp",EDGE,"E5");var subQ4=makeQuery(id+"F0.imprint","INTERSECT",VERTEX,{"derivedFrom":[subQ1,subQ3]});Q195=makeQuery(id+"F0.imprint","IMPRINT",FACE,{"disambiguationData":[TD([[makeQuery(id+"F0.imprint","IMPRINT",EDGE,{"disambiguationData":[TD([[subQ4,1.0]])],"derivedFrom":subQ3}),1.0]])]});}
            var Q196;
            {var subQ0=sQuery(id+"F0.wireOp",EDGE,"E40");var subQ1=sQuery(id+"F0.wireOp",EDGE,"E1");var subQ2=makeQuery(id+"F0.imprint","INTERSECT",VERTEX,{"derivedFrom":[subQ1,subQ0]});Q196=makeQuery(id+"F0.imprint","IMPRINT",FACE,{"disambiguationData":[TD([[makeQuery(id+"F0.imprint","IMPRINT",EDGE,{"disambiguationData":[TD([[subQ2,-1.0]])],"derivedFrom":subQ1}),1.0]])]});}
            var Q197;
            {var subQ0=sQuery(id+"F0.wireOp",EDGE,"E46");var subQ1=sQuery(id+"F0.wireOp",EDGE,"E23");var subQ2=makeQuery(id+"F0.imprint","INTERSECT",VERTEX,{"derivedFrom":[subQ1,subQ0]});Q197=makeQuery(id+"F0.imprint","IMPRINT",FACE,{"disambiguationData":[TD([[makeQuery(id+"F0.imprint","IMPRINT",EDGE,{"disambiguationData":[TD([[subQ2,-1.0]])],"derivedFrom":subQ1}),1.0]])]});}
            var Q198;
            {var subQ1=sQuery(id+"F0.wireOp",EDGE,"E10");var subQ7=sQuery(id+"F0.wireOp",EDGE,"E33");var subQ8=makeQuery(id+"F0.imprint","INTERSECT",VERTEX,{"derivedFrom":[subQ1,subQ7]});Q198=makeQuery(id+"F0.imprint","IMPRINT",FACE,{"disambiguationData":[TD([[makeQuery(id+"F0.imprint","IMPRINT",EDGE,{"disambiguationData":[TD([[subQ8,-1.0]])],"derivedFrom":subQ1}),1.0]])]});}
            var Q199;
            {var subQ0=sQuery(id+"F0.wireOp",EDGE,"E24");var subQ1=sQuery(id+"F0.wireOp",EDGE,"E17");var subQ2=makeQuery(id+"F0.imprint","INTERSECT",VERTEX,{"derivedFrom":[subQ1,subQ0]});Q199=makeQuery(id+"F0.imprint","IMPRINT",FACE,{"disambiguationData":[TD([[makeQuery(id+"F0.imprint","IMPRINT",EDGE,{"disambiguationData":[TD([[subQ2,-1.0]])],"derivedFrom":subQ1}),-1.0]])]});}
            var Q200;
            {var subQ0=sQuery(id+"F0.wireOp",EDGE,"E27");var subQ1=sQuery(id+"F0.wireOp",EDGE,"E19");var subQ2=makeQuery(id+"F0.imprint","INTERSECT",VERTEX,{"derivedFrom":[subQ1,subQ0]});Q200=makeQuery(id+"F0.imprint","IMPRINT",FACE,{"disambiguationData":[TD([[makeQuery(id+"F0.imprint","IMPRINT",EDGE,{"disambiguationData":[TD([[subQ2,-1.0]])],"derivedFrom":subQ1}),-1.0]])]});}
            var Q201;
            {var subQ0=sQuery(id+"F0.wireOp",EDGE,"E39");var subQ1=sQuery(id+"F0.wireOp",EDGE,"E21");var subQ2=makeQuery(id+"F0.imprint","INTERSECT",VERTEX,{"derivedFrom":[subQ1,subQ0]});Q201=makeQuery(id+"F0.imprint","IMPRINT",FACE,{"disambiguationData":[TD([[makeQuery(id+"F0.imprint","IMPRINT",EDGE,{"disambiguationData":[TD([[subQ2,-1.0]])],"derivedFrom":subQ1}),-1.0]])]});}
            var Q202;
            {var subQ3=sQuery(id+"F0.wireOp",EDGE,"E41");var subQ5=sQuery(id+"F0.wireOp",EDGE,"E0.bottom");var subQ6=makeQuery(id+"F0.imprint","INTERSECT",VERTEX,{"derivedFrom":[subQ5,subQ3]});Q202=makeQuery(id+"F0.imprint","IMPRINT",FACE,{"disambiguationData":[TD([[makeQuery(id+"F0.imprint","IMPRINT",EDGE,{"disambiguationData":[TD([[subQ6,-1.0]])],"derivedFrom":subQ5}),1.0]])]});}
            var Q203;
            {var subQ0=sQuery(id+"F0.wireOp",EDGE,"E27");var subQ1=sQuery(id+"F0.wireOp",EDGE,"E0.right");var subQ2=makeQuery(id+"F0.imprint","INTERSECT",VERTEX,{"derivedFrom":[subQ1,subQ0]});Q203=makeQuery(id+"F0.imprint","IMPRINT",FACE,{"disambiguationData":[TD([[makeQuery(id+"F0.imprint","IMPRINT",EDGE,{"disambiguationData":[TD([[subQ2,-1.0]])],"derivedFrom":subQ1}),1.0]])]});}
            var Q204;
            {var subQ0=sQuery(id+"F0.wireOp",EDGE,"E50");var subQ1=sQuery(id+"F0.wireOp",EDGE,"E1");var subQ2=makeQuery(id+"F0.imprint","INTERSECT",VERTEX,{"derivedFrom":[subQ1,subQ0]});Q204=makeQuery(id+"F0.imprint","IMPRINT",FACE,{"disambiguationData":[TD([[makeQuery(id+"F0.imprint","IMPRINT",EDGE,{"disambiguationData":[TD([[subQ2,-1.0]])],"derivedFrom":subQ1}),-1.0]])]});}
            var Q205;
            {var subQ0=sQuery(id+"F0.wireOp",EDGE,"E25");var subQ1=sQuery(id+"F0.wireOp",EDGE,"E4");var subQ2=makeQuery(id+"F0.imprint","INTERSECT",VERTEX,{"derivedFrom":[subQ1,subQ0]});Q205=makeQuery(id+"F0.imprint","IMPRINT",FACE,{"disambiguationData":[TD([[makeQuery(id+"F0.imprint","IMPRINT",EDGE,{"disambiguationData":[TD([[subQ2,-1.0]])],"derivedFrom":subQ1}),1.0]])]});}
            var Q206;
            {var subQ0=sQuery(id+"F0.wireOp",EDGE,"E39");var subQ1=sQuery(id+"F0.wireOp",EDGE,"E5");var subQ2=makeQuery(id+"F0.imprint","INTERSECT",VERTEX,{"derivedFrom":[subQ1,subQ0]});Q206=makeQuery(id+"F0.imprint","IMPRINT",FACE,{"disambiguationData":[TD([[makeQuery(id+"F0.imprint","IMPRINT",EDGE,{"disambiguationData":[TD([[subQ2,-1.0]])],"derivedFrom":subQ1}),1.0]])]});}
            var Q207;
            {var subQ1=sQuery(id+"F0.wireOp",EDGE,"E6");var subQ5=sQuery(id+"F0.wireOp",EDGE,"E37");var subQ6=makeQuery(id+"F0.imprint","INTERSECT",VERTEX,{"derivedFrom":[subQ1,subQ5]});Q207=makeQuery(id+"F0.imprint","IMPRINT",FACE,{"disambiguationData":[TD([[makeQuery(id+"F0.imprint","IMPRINT",EDGE,{"disambiguationData":[TD([[subQ6,-1.0]])],"derivedFrom":subQ1}),1.0]])]});}
            var Q208;
            {var subQ0=sQuery(id+"F0.wireOp",EDGE,"E26");var subQ1=sQuery(id+"F0.wireOp",EDGE,"E21");var subQ2=makeQuery(id+"F0.imprint","INTERSECT",VERTEX,{"derivedFrom":[subQ1,subQ0]});Q208=makeQuery(id+"F0.imprint","IMPRINT",FACE,{"disambiguationData":[TD([[makeQuery(id+"F0.imprint","IMPRINT",EDGE,{"disambiguationData":[TD([[subQ2,-1.0]])],"derivedFrom":subQ1}),-1.0]])]});}
            var Q209;
            {var subQ3=sQuery(id+"F0.wireOp",EDGE,"E17");var subQ7=sQuery(id+"F0.wireOp",EDGE,"E0.bottom");var subQ8=makeQuery(id+"F0.imprint","INTERSECT",VERTEX,{"derivedFrom":[subQ7,subQ3]});Q209=makeQuery(id+"F0.imprint","IMPRINT",FACE,{"disambiguationData":[TD([[makeQuery(id+"F0.imprint","IMPRINT",EDGE,{"disambiguationData":[TD([[subQ8,1.0]])],"derivedFrom":subQ7}),1.0]])]});}
            var Q210;
            {var subQ1=sQuery(id+"F0.wireOp",EDGE,"E14");var subQ5=sQuery(id+"F0.wireOp",EDGE,"E29");var subQ6=makeQuery(id+"F0.imprint","INTERSECT",VERTEX,{"derivedFrom":[subQ1,subQ5]});Q210=makeQuery(id+"F0.imprint","IMPRINT",FACE,{"disambiguationData":[TD([[makeQuery(id+"F0.imprint","IMPRINT",EDGE,{"disambiguationData":[TD([[subQ6,-1.0]])],"derivedFrom":subQ1}),1.0]])]});}
            var Q211;
            {var subQ0=sQuery(id+"F0.wireOp",EDGE,"E28");var subQ1=sQuery(id+"F0.wireOp",EDGE,"E17");var subQ2=makeQuery(id+"F0.imprint","INTERSECT",VERTEX,{"derivedFrom":[subQ1,subQ0]});Q211=makeQuery(id+"F0.imprint","IMPRINT",FACE,{"disambiguationData":[TD([[makeQuery(id+"F0.imprint","IMPRINT",EDGE,{"disambiguationData":[TD([[subQ2,-1.0]])],"derivedFrom":subQ1}),-1.0]])]});}
            var Q212;
            {var subQ0=sQuery(id+"F0.wireOp",EDGE,"E42");var subQ1=sQuery(id+"F0.wireOp",EDGE,"E20");var subQ2=makeQuery(id+"F0.imprint","INTERSECT",VERTEX,{"derivedFrom":[subQ1,subQ0]});Q212=makeQuery(id+"F0.imprint","IMPRINT",FACE,{"disambiguationData":[TD([[makeQuery(id+"F0.imprint","IMPRINT",EDGE,{"disambiguationData":[TD([[subQ2,-1.0]])],"derivedFrom":subQ1}),-1.0]])]});}
            var Q213;
            {var subQ0=sQuery(id+"F0.wireOp",EDGE,"E29");var subQ1=sQuery(id+"F0.wireOp",EDGE,"E7");var subQ2=makeQuery(id+"F0.imprint","INTERSECT",VERTEX,{"derivedFrom":[subQ1,subQ0]});Q213=makeQuery(id+"F0.imprint","IMPRINT",FACE,{"disambiguationData":[TD([[makeQuery(id+"F0.imprint","IMPRINT",EDGE,{"disambiguationData":[TD([[subQ2,-1.0]])],"derivedFrom":subQ1}),1.0]])]});}
            var Q214;
            {var subQ0=sQuery(id+"F0.wireOp",EDGE,"E32");var subQ1=sQuery(id+"F0.wireOp",EDGE,"E9");var subQ2=makeQuery(id+"F0.imprint","INTERSECT",VERTEX,{"derivedFrom":[subQ1,subQ0]});Q214=makeQuery(id+"F0.imprint","IMPRINT",FACE,{"disambiguationData":[TD([[makeQuery(id+"F0.imprint","IMPRINT",EDGE,{"disambiguationData":[TD([[subQ2,-1.0]])],"derivedFrom":subQ1}),1.0]])]});}
            var Q215;
            {var subQ0=sQuery(id+"F0.wireOp",EDGE,"E40");var subQ1=sQuery(id+"F0.wireOp",EDGE,"E4");var subQ2=makeQuery(id+"F0.imprint","INTERSECT",VERTEX,{"derivedFrom":[subQ1,subQ0]});Q215=makeQuery(id+"F0.imprint","IMPRINT",FACE,{"disambiguationData":[TD([[makeQuery(id+"F0.imprint","IMPRINT",EDGE,{"disambiguationData":[TD([[subQ2,-1.0]])],"derivedFrom":subQ1}),1.0]])]});}
            var Q216;
            {var subQ0=sQuery(id+"F0.wireOp",EDGE,"E43");var subQ1=sQuery(id+"F0.wireOp",EDGE,"E5");var subQ2=makeQuery(id+"F0.imprint","INTERSECT",VERTEX,{"derivedFrom":[subQ1,subQ0]});Q216=makeQuery(id+"F0.imprint","IMPRINT",FACE,{"disambiguationData":[TD([[makeQuery(id+"F0.imprint","IMPRINT",EDGE,{"disambiguationData":[TD([[subQ2,-1.0]])],"derivedFrom":subQ1}),1.0]])]});}
            var Q217;
            {var subQ0=sQuery(id+"F0.wireOp",EDGE,"E34");var subQ1=sQuery(id+"F0.wireOp",EDGE,"E5");var subQ2=makeQuery(id+"F0.imprint","INTERSECT",VERTEX,{"derivedFrom":[subQ1,subQ0]});Q217=makeQuery(id+"F0.imprint","IMPRINT",FACE,{"disambiguationData":[TD([[makeQuery(id+"F0.imprint","IMPRINT",EDGE,{"disambiguationData":[TD([[subQ2,-1.0]])],"derivedFrom":subQ1}),1.0]])]});}
            var Q218;
            {var subQ0=sQuery(id+"F0.wireOp",EDGE,"E31");var subQ1=sQuery(id+"F0.wireOp",EDGE,"E6");var subQ2=makeQuery(id+"F0.imprint","INTERSECT",VERTEX,{"derivedFrom":[subQ1,subQ0]});Q218=makeQuery(id+"F0.imprint","IMPRINT",FACE,{"disambiguationData":[TD([[makeQuery(id+"F0.imprint","IMPRINT",EDGE,{"disambiguationData":[TD([[subQ2,-1.0]])],"derivedFrom":subQ1}),1.0]])]});}
            var Q219;
            {var subQ0=sQuery(id+"F0.wireOp",EDGE,"E23");var subQ1=sQuery(id+"F0.wireOp",EDGE,"E1");var subQ2=makeQuery(id+"F0.imprint","INTERSECT",VERTEX,{"derivedFrom":[subQ1,subQ0]});Q219=makeQuery(id+"F0.imprint","IMPRINT",FACE,{"disambiguationData":[TD([[makeQuery(id+"F0.imprint","IMPRINT",EDGE,{"disambiguationData":[TD([[subQ2,-1.0]])],"derivedFrom":subQ1}),1.0]])]});}
            var Q220;
            {var subQ0=sQuery(id+"F0.wireOp",EDGE,"E31");var subQ1=sQuery(id+"F0.wireOp",EDGE,"E1");var subQ2=makeQuery(id+"F0.imprint","INTERSECT",VERTEX,{"derivedFrom":[subQ1,subQ0]});Q220=makeQuery(id+"F0.imprint","IMPRINT",FACE,{"disambiguationData":[TD([[makeQuery(id+"F0.imprint","IMPRINT",EDGE,{"disambiguationData":[TD([[subQ2,-1.0]])],"derivedFrom":subQ1}),1.0]])]});}
            var Q221;
            {var subQ0=sQuery(id+"F0.wireOp",EDGE,"E27");var subQ1=sQuery(id+"F0.wireOp",EDGE,"E2");var subQ2=makeQuery(id+"F0.imprint","INTERSECT",VERTEX,{"derivedFrom":[subQ1,subQ0]});Q221=makeQuery(id+"F0.imprint","IMPRINT",FACE,{"disambiguationData":[TD([[makeQuery(id+"F0.imprint","IMPRINT",EDGE,{"disambiguationData":[TD([[subQ2,-1.0]])],"derivedFrom":subQ1}),1.0]])]});}
            var Q222;
            {var subQ0=sQuery(id+"F0.wireOp",EDGE,"E24");var subQ1=sQuery(id+"F0.wireOp",EDGE,"E3");var subQ2=makeQuery(id+"F0.imprint","INTERSECT",VERTEX,{"derivedFrom":[subQ1,subQ0]});Q222=makeQuery(id+"F0.imprint","IMPRINT",FACE,{"disambiguationData":[TD([[makeQuery(id+"F0.imprint","IMPRINT",EDGE,{"disambiguationData":[TD([[subQ2,-1.0]])],"derivedFrom":subQ1}),1.0]])]});}
            var Q223;
            {var subQ0=sQuery(id+"F0.wireOp",EDGE,"E49");var subQ1=sQuery(id+"F0.wireOp",EDGE,"E0.left");var subQ2=makeQuery(id+"F0.imprint","INTERSECT",VERTEX,{"derivedFrom":[subQ1,subQ0]});Q223=makeQuery(id+"F0.imprint","IMPRINT",FACE,{"disambiguationData":[TD([[makeQuery(id+"F0.imprint","IMPRINT",EDGE,{"disambiguationData":[TD([[subQ2,1.0]])],"derivedFrom":subQ1}),-1.0]])]});}
            var Q224;
            {var subQ0=sQuery(id+"F0.wireOp",EDGE,"E45");var subQ1=sQuery(id+"F0.wireOp",EDGE,"E0.right");var subQ2=makeQuery(id+"F0.imprint","INTERSECT",VERTEX,{"derivedFrom":[subQ1,subQ0]});Q224=makeQuery(id+"F0.imprint","IMPRINT",FACE,{"disambiguationData":[TD([[makeQuery(id+"F0.imprint","IMPRINT",EDGE,{"disambiguationData":[TD([[subQ2,1.0]])],"derivedFrom":subQ1}),1.0]])]});}
            var Q225;
            {var subQ0=sQuery(id+"F0.wireOp",EDGE,"E50");var subQ1=sQuery(id+"F0.wireOp",EDGE,"E1");var subQ2=makeQuery(id+"F0.imprint","INTERSECT",VERTEX,{"derivedFrom":[subQ1,subQ0]});Q225=makeQuery(id+"F0.imprint","IMPRINT",FACE,{"disambiguationData":[TD([[makeQuery(id+"F0.imprint","IMPRINT",EDGE,{"disambiguationData":[TD([[subQ2,-1.0]])],"derivedFrom":subQ1}),1.0]])]});}
            var Q226;
            {var subQ0=sQuery(id+"F0.wireOp",EDGE,"E25");var subQ1=sQuery(id+"F0.wireOp",EDGE,"E21");var subQ2=makeQuery(id+"F0.imprint","INTERSECT",VERTEX,{"derivedFrom":[subQ1,subQ0]});Q226=makeQuery(id+"F0.imprint","IMPRINT",FACE,{"disambiguationData":[TD([[makeQuery(id+"F0.imprint","IMPRINT",EDGE,{"disambiguationData":[TD([[subQ2,-1.0]])],"derivedFrom":subQ1}),-1.0]])]});}
            var Q227;
            {var subQ0=sQuery(id+"F0.wireOp",EDGE,"E46");var subQ1=sQuery(id+"F0.wireOp",EDGE,"E39");var subQ2=makeQuery(id+"F0.imprint","INTERSECT",VERTEX,{"derivedFrom":[subQ1,subQ0]});Q227=makeQuery(id+"F0.imprint","IMPRINT",FACE,{"disambiguationData":[TD([[makeQuery(id+"F0.imprint","IMPRINT",EDGE,{"disambiguationData":[TD([[subQ2,-1.0]])],"derivedFrom":subQ1}),1.0]])]});}
            var Q228;
            {var subQ1=sQuery(id+"F0.wireOp",EDGE,"E13");var subQ5=sQuery(id+"F0.wireOp",EDGE,"E30");var subQ6=makeQuery(id+"F0.imprint","INTERSECT",VERTEX,{"derivedFrom":[subQ1,subQ5]});Q228=makeQuery(id+"F0.imprint","IMPRINT",FACE,{"disambiguationData":[TD([[makeQuery(id+"F0.imprint","IMPRINT",EDGE,{"disambiguationData":[TD([[subQ6,-1.0]])],"derivedFrom":subQ1}),1.0]])]});}
            var Q229;
            {var subQ0=sQuery(id+"F0.wireOp",EDGE,"E27");var subQ1=sQuery(id+"F0.wireOp",EDGE,"E1");var subQ2=makeQuery(id+"F0.imprint","INTERSECT",VERTEX,{"derivedFrom":[subQ1,subQ0]});Q229=makeQuery(id+"F0.imprint","IMPRINT",FACE,{"disambiguationData":[TD([[makeQuery(id+"F0.imprint","IMPRINT",EDGE,{"disambiguationData":[TD([[subQ2,-1.0]])],"derivedFrom":subQ1}),1.0]])]});}
            var Q230;
            {var subQ0=sQuery(id+"F0.wireOp",EDGE,"E27");var subQ1=sQuery(id+"F0.wireOp",EDGE,"E18");var subQ2=makeQuery(id+"F0.imprint","INTERSECT",VERTEX,{"derivedFrom":[subQ1,subQ0]});Q230=makeQuery(id+"F0.imprint","IMPRINT",FACE,{"disambiguationData":[TD([[makeQuery(id+"F0.imprint","IMPRINT",EDGE,{"disambiguationData":[TD([[subQ2,-1.0]])],"derivedFrom":subQ1}),-1.0]])]});}
            var Q231;
            {var subQ0=sQuery(id+"F0.wireOp",EDGE,"E28");var subQ1=sQuery(id+"F0.wireOp",EDGE,"E7");var subQ2=makeQuery(id+"F0.imprint","INTERSECT",VERTEX,{"derivedFrom":[subQ1,subQ0]});Q231=makeQuery(id+"F0.imprint","IMPRINT",FACE,{"disambiguationData":[TD([[makeQuery(id+"F0.imprint","IMPRINT",EDGE,{"disambiguationData":[TD([[subQ2,-1.0]])],"derivedFrom":subQ1}),1.0]])]});}
            var Q232;
            {var subQ0=sQuery(id+"F0.wireOp",EDGE,"E29");var subQ1=sQuery(id+"F0.wireOp",EDGE,"E8");var subQ2=makeQuery(id+"F0.imprint","INTERSECT",VERTEX,{"derivedFrom":[subQ1,subQ0]});Q232=makeQuery(id+"F0.imprint","IMPRINT",FACE,{"disambiguationData":[TD([[makeQuery(id+"F0.imprint","IMPRINT",EDGE,{"disambiguationData":[TD([[subQ2,-1.0]])],"derivedFrom":subQ1}),1.0]])]});}
            var Q233;
            {var subQ0=sQuery(id+"F0.wireOp",EDGE,"E44");var subQ1=sQuery(id+"F0.wireOp",EDGE,"E3");var subQ2=makeQuery(id+"F0.imprint","INTERSECT",VERTEX,{"derivedFrom":[subQ1,subQ0]});Q233=makeQuery(id+"F0.imprint","IMPRINT",FACE,{"disambiguationData":[TD([[makeQuery(id+"F0.imprint","IMPRINT",EDGE,{"disambiguationData":[TD([[subQ2,-1.0]])],"derivedFrom":subQ1}),1.0]])]});}
            var Q234;
            {var subQ0=sQuery(id+"F0.wireOp",EDGE,"E44");var subQ1=sQuery(id+"F0.wireOp",EDGE,"E5");var subQ2=makeQuery(id+"F0.imprint","INTERSECT",VERTEX,{"derivedFrom":[subQ1,subQ0]});Q234=makeQuery(id+"F0.imprint","IMPRINT",FACE,{"disambiguationData":[TD([[makeQuery(id+"F0.imprint","IMPRINT",EDGE,{"disambiguationData":[TD([[subQ2,-1.0]])],"derivedFrom":subQ1}),1.0]])]});}
            var Q235;
            {var subQ0=sQuery(id+"F0.wireOp",EDGE,"E42");var subQ1=sQuery(id+"F0.wireOp",EDGE,"E2");var subQ2=makeQuery(id+"F0.imprint","INTERSECT",VERTEX,{"derivedFrom":[subQ1,subQ0]});Q235=makeQuery(id+"F0.imprint","IMPRINT",FACE,{"disambiguationData":[TD([[makeQuery(id+"F0.imprint","IMPRINT",EDGE,{"disambiguationData":[TD([[subQ2,-1.0]])],"derivedFrom":subQ1}),1.0]])]});}
            var Q236;
            {var subQ0=sQuery(id+"F0.wireOp",EDGE,"E42");var subQ1=sQuery(id+"F0.wireOp",EDGE,"E18");var subQ2=makeQuery(id+"F0.imprint","INTERSECT",VERTEX,{"derivedFrom":[subQ1,subQ0]});Q236=makeQuery(id+"F0.imprint","IMPRINT",FACE,{"disambiguationData":[TD([[makeQuery(id+"F0.imprint","IMPRINT",EDGE,{"disambiguationData":[TD([[subQ2,-1.0]])],"derivedFrom":subQ1}),-1.0]])]});}
            var Q237;
            {var subQ0=sQuery(id+"F0.wireOp",EDGE,"E33");var subQ1=sQuery(id+"F0.wireOp",EDGE,"E5");var subQ2=makeQuery(id+"F0.imprint","INTERSECT",VERTEX,{"derivedFrom":[subQ1,subQ0]});Q237=makeQuery(id+"F0.imprint","IMPRINT",FACE,{"disambiguationData":[TD([[makeQuery(id+"F0.imprint","IMPRINT",EDGE,{"disambiguationData":[TD([[subQ2,-1.0]])],"derivedFrom":subQ1}),1.0]])]});}
            var Q238;
            {var subQ0=sQuery(id+"F0.wireOp",EDGE,"E3");var subQ1=sQuery(id+"F0.wireOp",EDGE,"E0.left");var subQ2=makeQuery(id+"F0.imprint","INTERSECT",VERTEX,{"derivedFrom":[subQ1,subQ0]});Q238=makeQuery(id+"F0.imprint","IMPRINT",FACE,{"disambiguationData":[TD([[makeQuery(id+"F0.imprint","IMPRINT",EDGE,{"disambiguationData":[TD([[subQ2,-1.0]])],"derivedFrom":subQ1}),-1.0]])]});}
            var Q239;
            {var subQ0=sQuery(id+"F0.wireOp",EDGE,"E42");var subQ1=sQuery(id+"F0.wireOp",EDGE,"E17");var subQ2=makeQuery(id+"F0.imprint","INTERSECT",VERTEX,{"derivedFrom":[subQ1,subQ0]});Q239=makeQuery(id+"F0.imprint","IMPRINT",FACE,{"disambiguationData":[TD([[makeQuery(id+"F0.imprint","IMPRINT",EDGE,{"disambiguationData":[TD([[subQ2,-1.0]])],"derivedFrom":subQ1}),-1.0]])]});}
            var Q240;
            {var subQ0=sQuery(id+"F0.wireOp",EDGE,"E25");var subQ1=sQuery(id+"F0.wireOp",EDGE,"E0.right");var subQ2=makeQuery(id+"F0.imprint","INTERSECT",VERTEX,{"derivedFrom":[subQ1,subQ0]});Q240=makeQuery(id+"F0.imprint","IMPRINT",FACE,{"disambiguationData":[TD([[makeQuery(id+"F0.imprint","IMPRINT",EDGE,{"disambiguationData":[TD([[subQ2,-1.0]])],"derivedFrom":subQ1}),1.0]])]});}
            var Q241;
            {var subQ0=sQuery(id+"F0.wireOp",EDGE,"E24");var subQ1=sQuery(id+"F0.wireOp",EDGE,"E21");var subQ2=makeQuery(id+"F0.imprint","INTERSECT",VERTEX,{"derivedFrom":[subQ1,subQ0]});Q241=makeQuery(id+"F0.imprint","IMPRINT",FACE,{"disambiguationData":[TD([[makeQuery(id+"F0.imprint","IMPRINT",EDGE,{"disambiguationData":[TD([[subQ2,-1.0]])],"derivedFrom":subQ1}),-1.0]])]});}
            var Q242;
            {var subQ0=sQuery(id+"F0.wireOp",EDGE,"E46");var subQ1=sQuery(id+"F0.wireOp",EDGE,"E25");var subQ2=makeQuery(id+"F0.imprint","INTERSECT",VERTEX,{"derivedFrom":[subQ1,subQ0]});Q242=makeQuery(id+"F0.imprint","IMPRINT",FACE,{"disambiguationData":[TD([[makeQuery(id+"F0.imprint","IMPRINT",EDGE,{"disambiguationData":[TD([[subQ2,-1.0]])],"derivedFrom":subQ1}),-1.0]])]});}
            var Q243;
            {var subQ1=sQuery(id+"F0.wireOp",EDGE,"E12");var subQ5=sQuery(id+"F0.wireOp",EDGE,"E31");var subQ6=makeQuery(id+"F0.imprint","INTERSECT",VERTEX,{"derivedFrom":[subQ1,subQ5]});Q243=makeQuery(id+"F0.imprint","IMPRINT",FACE,{"disambiguationData":[TD([[makeQuery(id+"F0.imprint","IMPRINT",EDGE,{"disambiguationData":[TD([[subQ6,-1.0]])],"derivedFrom":subQ1}),1.0]])]});}
            var Q244;
            {var subQ0=sQuery(id+"F0.wireOp",EDGE,"E26");var subQ1=sQuery(id+"F0.wireOp",EDGE,"E17");var subQ2=makeQuery(id+"F0.imprint","INTERSECT",VERTEX,{"derivedFrom":[subQ1,subQ0]});Q244=makeQuery(id+"F0.imprint","IMPRINT",FACE,{"disambiguationData":[TD([[makeQuery(id+"F0.imprint","IMPRINT",EDGE,{"disambiguationData":[TD([[subQ2,-1.0]])],"derivedFrom":subQ1}),-1.0]])]});}
            var Q245;
            {var subQ0=sQuery(id+"F0.wireOp",EDGE,"E29");var subQ1=sQuery(id+"F0.wireOp",EDGE,"E19");var subQ2=makeQuery(id+"F0.imprint","INTERSECT",VERTEX,{"derivedFrom":[subQ1,subQ0]});Q245=makeQuery(id+"F0.imprint","IMPRINT",FACE,{"disambiguationData":[TD([[makeQuery(id+"F0.imprint","IMPRINT",EDGE,{"disambiguationData":[TD([[subQ2,-1.0]])],"derivedFrom":subQ1}),-1.0]])]});}
            var Q246;
            {var subQ0=sQuery(id+"F0.wireOp",EDGE,"E30");var subQ1=sQuery(id+"F0.wireOp",EDGE,"E9");var subQ2=makeQuery(id+"F0.imprint","INTERSECT",VERTEX,{"derivedFrom":[subQ1,subQ0]});Q246=makeQuery(id+"F0.imprint","IMPRINT",FACE,{"disambiguationData":[TD([[makeQuery(id+"F0.imprint","IMPRINT",EDGE,{"disambiguationData":[TD([[subQ2,-1.0]])],"derivedFrom":subQ1}),1.0]])]});}
            var Q247;
            {var subQ0=sQuery(id+"F0.wireOp",EDGE,"E7");var subQ1=sQuery(id+"F0.wireOp",EDGE,"E0.left");var subQ2=makeQuery(id+"F0.imprint","INTERSECT",VERTEX,{"derivedFrom":[subQ1,subQ0]});Q247=makeQuery(id+"F0.imprint","IMPRINT",FACE,{"disambiguationData":[TD([[makeQuery(id+"F0.imprint","IMPRINT",EDGE,{"disambiguationData":[TD([[subQ2,-1.0]])],"derivedFrom":subQ1}),-1.0]])]});}
            var Q248;
            {var subQ0=sQuery(id+"F0.wireOp",EDGE,"E33");var subQ1=sQuery(id+"F0.wireOp",EDGE,"E3");var subQ2=makeQuery(id+"F0.imprint","INTERSECT",VERTEX,{"derivedFrom":[subQ1,subQ0]});Q248=makeQuery(id+"F0.imprint","IMPRINT",FACE,{"disambiguationData":[TD([[makeQuery(id+"F0.imprint","IMPRINT",EDGE,{"disambiguationData":[TD([[subQ2,-1.0]])],"derivedFrom":subQ1}),1.0]])]});}
            var Q249;
            {var subQ0=sQuery(id+"F0.wireOp",EDGE,"E40");var subQ1=sQuery(id+"F0.wireOp",EDGE,"E17");var subQ2=makeQuery(id+"F0.imprint","INTERSECT",VERTEX,{"derivedFrom":[subQ1,subQ0]});Q249=makeQuery(id+"F0.imprint","IMPRINT",FACE,{"disambiguationData":[TD([[makeQuery(id+"F0.imprint","IMPRINT",EDGE,{"disambiguationData":[TD([[subQ2,-1.0]])],"derivedFrom":subQ1}),-1.0]])]});}
            var Q250;
            {var subQ0=sQuery(id+"F0.wireOp",EDGE,"E40");var subQ1=sQuery(id+"F0.wireOp",EDGE,"E18");var subQ2=makeQuery(id+"F0.imprint","INTERSECT",VERTEX,{"derivedFrom":[subQ1,subQ0]});Q250=makeQuery(id+"F0.imprint","IMPRINT",FACE,{"disambiguationData":[TD([[makeQuery(id+"F0.imprint","IMPRINT",EDGE,{"disambiguationData":[TD([[subQ2,-1.0]])],"derivedFrom":subQ1}),-1.0]])]});}
            var Q251;
            {var subQ0=sQuery(id+"F0.wireOp",EDGE,"E39");var subQ1=sQuery(id+"F0.wireOp",EDGE,"E7");var subQ2=makeQuery(id+"F0.imprint","INTERSECT",VERTEX,{"derivedFrom":[subQ1,subQ0]});Q251=makeQuery(id+"F0.imprint","IMPRINT",FACE,{"disambiguationData":[TD([[makeQuery(id+"F0.imprint","IMPRINT",EDGE,{"disambiguationData":[TD([[subQ2,-1.0]])],"derivedFrom":subQ1}),1.0]])]});}
            var Q252;
            {var subQ0=sQuery(id+"F0.wireOp",EDGE,"E23");var subQ1=sQuery(id+"F0.wireOp",EDGE,"E8");var subQ2=makeQuery(id+"F0.imprint","INTERSECT",VERTEX,{"derivedFrom":[subQ1,subQ0]});Q252=makeQuery(id+"F0.imprint","IMPRINT",FACE,{"disambiguationData":[TD([[makeQuery(id+"F0.imprint","IMPRINT",EDGE,{"disambiguationData":[TD([[subQ2,-1.0]])],"derivedFrom":subQ1}),1.0]])]});}
            var Q253;
            {var subQ0=sQuery(id+"F0.wireOp",EDGE,"E35");var subQ1=sQuery(id+"F0.wireOp",EDGE,"E0.right");var subQ2=makeQuery(id+"F0.imprint","INTERSECT",VERTEX,{"derivedFrom":[subQ1,subQ0]});Q253=makeQuery(id+"F0.imprint","IMPRINT",FACE,{"disambiguationData":[TD([[makeQuery(id+"F0.imprint","IMPRINT",EDGE,{"disambiguationData":[TD([[subQ2,-1.0]])],"derivedFrom":subQ1}),1.0]])]});}
            var Q254;
            {var subQ0=sQuery(id+"F0.wireOp",EDGE,"E42");var subQ1=sQuery(id+"F0.wireOp",EDGE,"E1");var subQ2=makeQuery(id+"F0.imprint","INTERSECT",VERTEX,{"derivedFrom":[subQ1,subQ0]});Q254=makeQuery(id+"F0.imprint","IMPRINT",FACE,{"disambiguationData":[TD([[makeQuery(id+"F0.imprint","IMPRINT",EDGE,{"disambiguationData":[TD([[subQ2,-1.0]])],"derivedFrom":subQ1}),-1.0]])]});}
            var Q255;
            {var subQ0=sQuery(id+"F0.wireOp",EDGE,"E27");var subQ1=sQuery(id+"F0.wireOp",EDGE,"E1");var subQ2=makeQuery(id+"F0.imprint","INTERSECT",VERTEX,{"derivedFrom":[subQ1,subQ0]});Q255=makeQuery(id+"F0.imprint","IMPRINT",FACE,{"disambiguationData":[TD([[makeQuery(id+"F0.imprint","IMPRINT",EDGE,{"disambiguationData":[TD([[subQ2,-1.0]])],"derivedFrom":subQ1}),-1.0]])]});}
            var Q256;
            {var subQ0=sQuery(id+"F0.wireOp",EDGE,"E13");var subQ1=sQuery(id+"F0.wireOp",EDGE,"E0.left");var subQ2=makeQuery(id+"F0.imprint","INTERSECT",VERTEX,{"derivedFrom":[subQ1,subQ0]});Q256=makeQuery(id+"F0.imprint","IMPRINT",FACE,{"disambiguationData":[TD([[makeQuery(id+"F0.imprint","IMPRINT",EDGE,{"disambiguationData":[TD([[subQ2,-1.0]])],"derivedFrom":subQ1}),-1.0]])]});}
            var Q257;
            {var subQ0=sQuery(id+"F0.wireOp",EDGE,"E23");var subQ1=sQuery(id+"F0.wireOp",EDGE,"E19");var subQ2=makeQuery(id+"F0.imprint","INTERSECT",VERTEX,{"derivedFrom":[subQ1,subQ0]});Q257=makeQuery(id+"F0.imprint","IMPRINT",FACE,{"disambiguationData":[TD([[makeQuery(id+"F0.imprint","IMPRINT",EDGE,{"disambiguationData":[TD([[subQ2,-1.0]])],"derivedFrom":subQ1}),-1.0]])]});}
            var Q258;
            {var subQ0=sQuery(id+"F0.wireOp",EDGE,"E27");var subQ1=sQuery(id+"F0.wireOp",EDGE,"E20");var subQ2=makeQuery(id+"F0.imprint","INTERSECT",VERTEX,{"derivedFrom":[subQ1,subQ0]});Q258=makeQuery(id+"F0.imprint","IMPRINT",FACE,{"disambiguationData":[TD([[makeQuery(id+"F0.imprint","IMPRINT",EDGE,{"disambiguationData":[TD([[subQ2,-1.0]])],"derivedFrom":subQ1}),-1.0]])]});}
            var Q259;
            {var subQ0=sQuery(id+"F0.wireOp",EDGE,"E48");var subQ1=sQuery(id+"F0.wireOp",EDGE,"E23");var subQ2=makeQuery(id+"F0.imprint","INTERSECT",VERTEX,{"derivedFrom":[subQ1,subQ0]});Q259=makeQuery(id+"F0.imprint","IMPRINT",FACE,{"disambiguationData":[TD([[makeQuery(id+"F0.imprint","IMPRINT",EDGE,{"disambiguationData":[TD([[subQ2,-1.0]])],"derivedFrom":subQ1}),-1.0]])]});}
            var Q260;
            {var subQ3=sQuery(id+"F0.wireOp",EDGE,"E40");var subQ7=sQuery(id+"F0.wireOp",EDGE,"E0.bottom");var subQ8=makeQuery(id+"F0.imprint","INTERSECT",VERTEX,{"derivedFrom":[subQ7,subQ3]});Q260=makeQuery(id+"F0.imprint","IMPRINT",FACE,{"disambiguationData":[TD([[makeQuery(id+"F0.imprint","IMPRINT",EDGE,{"disambiguationData":[TD([[subQ8,-1.0]])],"derivedFrom":subQ7}),1.0]])]});}
            var Q261;
            {var subQ0=sQuery(id+"F0.wireOp",EDGE,"E33");var subQ1=sQuery(id+"F0.wireOp",EDGE,"E0.right");var subQ2=makeQuery(id+"F0.imprint","INTERSECT",VERTEX,{"derivedFrom":[subQ1,subQ0]});Q261=makeQuery(id+"F0.imprint","IMPRINT",FACE,{"disambiguationData":[TD([[makeQuery(id+"F0.imprint","IMPRINT",EDGE,{"disambiguationData":[TD([[subQ2,-1.0]])],"derivedFrom":subQ1}),1.0]])]});}
            var Q262;
            {var subQ0=sQuery(id+"F0.wireOp",EDGE,"E41");var subQ1=sQuery(id+"F0.wireOp",EDGE,"E17");var subQ2=makeQuery(id+"F0.imprint","INTERSECT",VERTEX,{"derivedFrom":[subQ1,subQ0]});Q262=makeQuery(id+"F0.imprint","IMPRINT",FACE,{"disambiguationData":[TD([[makeQuery(id+"F0.imprint","IMPRINT",EDGE,{"disambiguationData":[TD([[subQ2,-1.0]])],"derivedFrom":subQ1}),-1.0]])]});}
            var Q263;
            {var subQ0=sQuery(id+"F0.wireOp",EDGE,"E23");var subQ1=sQuery(id+"F0.wireOp",EDGE,"E6");var subQ2=makeQuery(id+"F0.imprint","INTERSECT",VERTEX,{"derivedFrom":[subQ1,subQ0]});Q263=makeQuery(id+"F0.imprint","IMPRINT",FACE,{"disambiguationData":[TD([[makeQuery(id+"F0.imprint","IMPRINT",EDGE,{"disambiguationData":[TD([[subQ2,-1.0]])],"derivedFrom":subQ1}),1.0]])]});}
            var Q264;
            {var subQ0=sQuery(id+"F0.wireOp",EDGE,"E40");var subQ1=sQuery(id+"F0.wireOp",EDGE,"E7");var subQ2=makeQuery(id+"F0.imprint","INTERSECT",VERTEX,{"derivedFrom":[subQ1,subQ0]});Q264=makeQuery(id+"F0.imprint","IMPRINT",FACE,{"disambiguationData":[TD([[makeQuery(id+"F0.imprint","IMPRINT",EDGE,{"disambiguationData":[TD([[subQ2,-1.0]])],"derivedFrom":subQ1}),1.0]])]});}
            var Q265;
            {var subQ0=sQuery(id+"F0.wireOp",EDGE,"E49");var subQ1=sQuery(id+"F0.wireOp",EDGE,"E3");var subQ2=makeQuery(id+"F0.imprint","INTERSECT",VERTEX,{"derivedFrom":[subQ1,subQ0]});Q265=makeQuery(id+"F0.imprint","IMPRINT",FACE,{"disambiguationData":[TD([[makeQuery(id+"F0.imprint","IMPRINT",EDGE,{"disambiguationData":[TD([[subQ2,-1.0]])],"derivedFrom":subQ1}),1.0]])]});}
            var Q266;
            {var subQ0=sQuery(id+"F0.wireOp",EDGE,"E32");var subQ1=sQuery(id+"F0.wireOp",EDGE,"E3");var subQ2=makeQuery(id+"F0.imprint","INTERSECT",VERTEX,{"derivedFrom":[subQ1,subQ0]});Q266=makeQuery(id+"F0.imprint","IMPRINT",FACE,{"disambiguationData":[TD([[makeQuery(id+"F0.imprint","IMPRINT",EDGE,{"disambiguationData":[TD([[subQ2,-1.0]])],"derivedFrom":subQ1}),1.0]])]});}
            var Q267;
            {var subQ0=sQuery(id+"F0.wireOp",EDGE,"E29");var subQ1=sQuery(id+"F0.wireOp",EDGE,"E4");var subQ2=makeQuery(id+"F0.imprint","INTERSECT",VERTEX,{"derivedFrom":[subQ1,subQ0]});Q267=makeQuery(id+"F0.imprint","IMPRINT",FACE,{"disambiguationData":[TD([[makeQuery(id+"F0.imprint","IMPRINT",EDGE,{"disambiguationData":[TD([[subQ2,-1.0]])],"derivedFrom":subQ1}),1.0]])]});}
            var Q268;
            {var subQ0=sQuery(id+"F0.wireOp",EDGE,"E26");var subQ1=sQuery(id+"F0.wireOp",EDGE,"E5");var subQ2=makeQuery(id+"F0.imprint","INTERSECT",VERTEX,{"derivedFrom":[subQ1,subQ0]});Q268=makeQuery(id+"F0.imprint","IMPRINT",FACE,{"disambiguationData":[TD([[makeQuery(id+"F0.imprint","IMPRINT",EDGE,{"disambiguationData":[TD([[subQ2,-1.0]])],"derivedFrom":subQ1}),1.0]])]});}
            var Q269;
            {var subQ0=sQuery(id+"F0.wireOp",EDGE,"E1");var subQ1=sQuery(id+"F0.wireOp",EDGE,"E0.right");var subQ2=makeQuery(id+"F0.imprint","INTERSECT",VERTEX,{"derivedFrom":[subQ1,subQ0]});Q269=makeQuery(id+"F0.imprint","IMPRINT",FACE,{"disambiguationData":[TD([[makeQuery(id+"F0.imprint","IMPRINT",EDGE,{"disambiguationData":[TD([[subQ2,-1.0]])],"derivedFrom":subQ1}),1.0]])]});}
            var Q270;
            {var subQ0=sQuery(id+"F0.wireOp",EDGE,"E42");var subQ1=sQuery(id+"F0.wireOp",EDGE,"E1");var subQ2=makeQuery(id+"F0.imprint","INTERSECT",VERTEX,{"derivedFrom":[subQ1,subQ0]});Q270=makeQuery(id+"F0.imprint","IMPRINT",FACE,{"disambiguationData":[TD([[makeQuery(id+"F0.imprint","IMPRINT",EDGE,{"disambiguationData":[TD([[subQ2,-1.0]])],"derivedFrom":subQ1}),1.0]])]});}
            var Q271;
            {var subQ0=sQuery(id+"F0.wireOp",EDGE,"E42");var subQ1=sQuery(id+"F0.wireOp",EDGE,"E7");var subQ2=makeQuery(id+"F0.imprint","INTERSECT",VERTEX,{"derivedFrom":[subQ1,subQ0]});Q271=makeQuery(id+"F0.imprint","IMPRINT",FACE,{"disambiguationData":[TD([[makeQuery(id+"F0.imprint","IMPRINT",EDGE,{"disambiguationData":[TD([[subQ2,-1.0]])],"derivedFrom":subQ1}),1.0]])]});}
            var Q272;
            {var subQ0=sQuery(id+"F0.wireOp",EDGE,"E35");var subQ1=sQuery(id+"F0.wireOp",EDGE,"E5");var subQ2=makeQuery(id+"F0.imprint","INTERSECT",VERTEX,{"derivedFrom":[subQ1,subQ0]});Q272=makeQuery(id+"F0.imprint","IMPRINT",FACE,{"disambiguationData":[TD([[makeQuery(id+"F0.imprint","IMPRINT",EDGE,{"disambiguationData":[TD([[subQ2,-1.0]])],"derivedFrom":subQ1}),1.0]])]});}
            var Q273;
            {var subQ0=sQuery(id+"F0.wireOp",EDGE,"E27");var subQ1=sQuery(id+"F0.wireOp",EDGE,"E17");var subQ2=makeQuery(id+"F0.imprint","INTERSECT",VERTEX,{"derivedFrom":[subQ1,subQ0]});Q273=makeQuery(id+"F0.imprint","IMPRINT",FACE,{"disambiguationData":[TD([[makeQuery(id+"F0.imprint","IMPRINT",EDGE,{"disambiguationData":[TD([[subQ2,-1.0]])],"derivedFrom":subQ1}),-1.0]])]});}
            var Q274;
            {var subQ0=sQuery(id+"F0.wireOp",EDGE,"E31");var subQ1=sQuery(id+"F0.wireOp",EDGE,"E9");var subQ2=makeQuery(id+"F0.imprint","INTERSECT",VERTEX,{"derivedFrom":[subQ1,subQ0]});Q274=makeQuery(id+"F0.imprint","IMPRINT",FACE,{"disambiguationData":[TD([[makeQuery(id+"F0.imprint","IMPRINT",EDGE,{"disambiguationData":[TD([[subQ2,-1.0]])],"derivedFrom":subQ1}),1.0]])]});}
            var Q275;
            {var subQ0=sQuery(id+"F0.wireOp",EDGE,"E23");var subQ1=sQuery(id+"F0.wireOp",EDGE,"E3");var subQ2=makeQuery(id+"F0.imprint","INTERSECT",VERTEX,{"derivedFrom":[subQ1,subQ0]});Q275=makeQuery(id+"F0.imprint","IMPRINT",FACE,{"disambiguationData":[TD([[makeQuery(id+"F0.imprint","IMPRINT",EDGE,{"disambiguationData":[TD([[subQ2,-1.0]])],"derivedFrom":subQ1}),1.0]])]});}
            var Q276;
            {var subQ0=sQuery(id+"F0.wireOp",EDGE,"E41");var subQ1=sQuery(id+"F0.wireOp",EDGE,"E0.bottom");var subQ2=makeQuery(id+"F0.imprint","INTERSECT",VERTEX,{"derivedFrom":[subQ1,subQ0]});Q276=makeQuery(id+"F0.imprint","IMPRINT",FACE,{"disambiguationData":[TD([[makeQuery(id+"F0.imprint","IMPRINT",EDGE,{"disambiguationData":[TD([[subQ2,1.0]])],"derivedFrom":subQ1}),1.0]])]});}
            var Q277;
            {var subQ0=sQuery(id+"F0.wireOp",EDGE,"E33");var subQ1=sQuery(id+"F0.wireOp",EDGE,"E11");var subQ2=makeQuery(id+"F0.imprint","INTERSECT",VERTEX,{"derivedFrom":[subQ1,subQ0]});Q277=makeQuery(id+"F0.imprint","IMPRINT",FACE,{"disambiguationData":[TD([[makeQuery(id+"F0.imprint","IMPRINT",EDGE,{"disambiguationData":[TD([[subQ2,-1.0]])],"derivedFrom":subQ1}),1.0]])]});}
            var Q278;
            {var subQ0=sQuery(id+"F0.wireOp",EDGE,"E17");var subQ1=sQuery(id+"F0.wireOp",EDGE,"E0.bottom");var subQ2=makeQuery(id+"F0.imprint","INTERSECT",VERTEX,{"derivedFrom":[subQ1,subQ0]});Q278=makeQuery(id+"F0.imprint","IMPRINT",FACE,{"disambiguationData":[TD([[makeQuery(id+"F0.imprint","IMPRINT",EDGE,{"disambiguationData":[TD([[subQ2,-1.0]])],"derivedFrom":subQ1}),1.0]])]});}
            var Q279;
            {var subQ0=sQuery(id+"F0.wireOp",EDGE,"E35");var subQ1=sQuery(id+"F0.wireOp",EDGE,"E9");var subQ2=makeQuery(id+"F0.imprint","INTERSECT",VERTEX,{"derivedFrom":[subQ1,subQ0]});Q279=makeQuery(id+"F0.imprint","IMPRINT",FACE,{"disambiguationData":[TD([[makeQuery(id+"F0.imprint","IMPRINT",EDGE,{"disambiguationData":[TD([[subQ2,-1.0]])],"derivedFrom":subQ1}),1.0]])]});}
            var Q280;
            {var subQ0=sQuery(id+"F0.wireOp",EDGE,"E29");var subQ1=sQuery(id+"F0.wireOp",EDGE,"E15");var subQ2=makeQuery(id+"F0.imprint","INTERSECT",VERTEX,{"derivedFrom":[subQ1,subQ0]});Q280=makeQuery(id+"F0.imprint","IMPRINT",FACE,{"disambiguationData":[TD([[makeQuery(id+"F0.imprint","IMPRINT",EDGE,{"disambiguationData":[TD([[subQ2,-1.0]])],"derivedFrom":subQ1}),1.0]])]});}
            var Q281;
            {var subQ0=sQuery(id+"F0.wireOp",EDGE,"E35");var subQ1=sQuery(id+"F0.wireOp",EDGE,"E10");var subQ2=makeQuery(id+"F0.imprint","INTERSECT",VERTEX,{"derivedFrom":[subQ1,subQ0]});Q281=makeQuery(id+"F0.imprint","IMPRINT",FACE,{"disambiguationData":[TD([[makeQuery(id+"F0.imprint","IMPRINT",EDGE,{"disambiguationData":[TD([[subQ2,1.0]])],"derivedFrom":subQ1}),-1.0]])]});}
            var Q282;
            {var subQ0=sQuery(id+"F0.wireOp",EDGE,"E39");var subQ1=sQuery(id+"F0.wireOp",EDGE,"E0.bottom");var subQ2=makeQuery(id+"F0.imprint","INTERSECT",VERTEX,{"derivedFrom":[subQ1,subQ0]});Q282=makeQuery(id+"F0.imprint","IMPRINT",FACE,{"disambiguationData":[TD([[makeQuery(id+"F0.imprint","IMPRINT",EDGE,{"disambiguationData":[TD([[subQ2,1.0]])],"derivedFrom":subQ1}),1.0]])]});}
            var Q283;
            {var subQ0=sQuery(id+"F0.wireOp",EDGE,"E36");var subQ1=sQuery(id+"F0.wireOp",EDGE,"E9");var subQ2=makeQuery(id+"F0.imprint","INTERSECT",VERTEX,{"derivedFrom":[subQ1,subQ0]});Q283=makeQuery(id+"F0.imprint","IMPRINT",FACE,{"disambiguationData":[TD([[makeQuery(id+"F0.imprint","IMPRINT",EDGE,{"disambiguationData":[TD([[subQ2,1.0]])],"derivedFrom":subQ1}),-1.0]])]});}
            var Q284;
            {var subQ0=sQuery(id+"F0.wireOp",EDGE,"E19");var subQ1=sQuery(id+"F0.wireOp",EDGE,"E0.bottom");var subQ2=makeQuery(id+"F0.imprint","INTERSECT",VERTEX,{"derivedFrom":[subQ1,subQ0]});Q284=makeQuery(id+"F0.imprint","IMPRINT",FACE,{"disambiguationData":[TD([[makeQuery(id+"F0.imprint","IMPRINT",EDGE,{"disambiguationData":[TD([[subQ2,-1.0]])],"derivedFrom":subQ1}),1.0]])]});}
            var Q285;
            {var subQ0=sQuery(id+"F0.wireOp",EDGE,"E21");var subQ1=sQuery(id+"F0.wireOp",EDGE,"E0.bottom");var subQ2=makeQuery(id+"F0.imprint","INTERSECT",VERTEX,{"derivedFrom":[subQ1,subQ0]});Q285=makeQuery(id+"F0.imprint","IMPRINT",FACE,{"disambiguationData":[TD([[makeQuery(id+"F0.imprint","IMPRINT",EDGE,{"disambiguationData":[TD([[subQ2,-1.0]])],"derivedFrom":subQ1}),1.0]])]});}
            var Q286;
            {var subQ0=sQuery(id+"F0.wireOp",EDGE,"E37");var subQ1=sQuery(id+"F0.wireOp",EDGE,"E7");var subQ2=makeQuery(id+"F0.imprint","INTERSECT",VERTEX,{"derivedFrom":[subQ1,subQ0]});Q286=makeQuery(id+"F0.imprint","IMPRINT",FACE,{"disambiguationData":[TD([[makeQuery(id+"F0.imprint","IMPRINT",EDGE,{"disambiguationData":[TD([[subQ2,-1.0]])],"derivedFrom":subQ1}),1.0]])]});}
            var Q287;
            {var subQ0=sQuery(id+"F0.wireOp",EDGE,"E31");var subQ1=sQuery(id+"F0.wireOp",EDGE,"E13");var subQ2=makeQuery(id+"F0.imprint","INTERSECT",VERTEX,{"derivedFrom":[subQ1,subQ0]});Q287=makeQuery(id+"F0.imprint","IMPRINT",FACE,{"disambiguationData":[TD([[makeQuery(id+"F0.imprint","IMPRINT",EDGE,{"disambiguationData":[TD([[subQ2,-1.0]])],"derivedFrom":subQ1}),1.0]])]});}
            var Q288;
            {var subQ0=sQuery(id+"F0.wireOp",EDGE,"E29");var subQ1=sQuery(id+"F0.wireOp",EDGE,"E16");var subQ2=makeQuery(id+"F0.imprint","INTERSECT",VERTEX,{"derivedFrom":[subQ1,subQ0]});Q288=makeQuery(id+"F0.imprint","IMPRINT",FACE,{"disambiguationData":[TD([[makeQuery(id+"F0.imprint","IMPRINT",EDGE,{"disambiguationData":[TD([[subQ2,1.0]])],"derivedFrom":subQ1}),-1.0]])]});}
            var Q289;
            {var subQ0=sQuery(id+"F0.wireOp",EDGE,"E30");var subQ1=sQuery(id+"F0.wireOp",EDGE,"E15");var subQ2=makeQuery(id+"F0.imprint","INTERSECT",VERTEX,{"derivedFrom":[subQ1,subQ0]});Q289=makeQuery(id+"F0.imprint","IMPRINT",FACE,{"disambiguationData":[TD([[makeQuery(id+"F0.imprint","IMPRINT",EDGE,{"disambiguationData":[TD([[subQ2,1.0]])],"derivedFrom":subQ1}),-1.0]])]});}
            var Q290;
            {var subQ0=sQuery(id+"F0.wireOp",EDGE,"E31");var subQ1=sQuery(id+"F0.wireOp",EDGE,"E14");var subQ2=makeQuery(id+"F0.imprint","INTERSECT",VERTEX,{"derivedFrom":[subQ1,subQ0]});Q290=makeQuery(id+"F0.imprint","IMPRINT",FACE,{"disambiguationData":[TD([[makeQuery(id+"F0.imprint","IMPRINT",EDGE,{"disambiguationData":[TD([[subQ2,1.0]])],"derivedFrom":subQ1}),-1.0]])]});}
            var Q291;
            {var subQ0=sQuery(id+"F0.wireOp",EDGE,"E32");var subQ1=sQuery(id+"F0.wireOp",EDGE,"E13");var subQ2=makeQuery(id+"F0.imprint","INTERSECT",VERTEX,{"derivedFrom":[subQ1,subQ0]});Q291=makeQuery(id+"F0.imprint","IMPRINT",FACE,{"disambiguationData":[TD([[makeQuery(id+"F0.imprint","IMPRINT",EDGE,{"disambiguationData":[TD([[subQ2,1.0]])],"derivedFrom":subQ1}),-1.0]])]});}
            var Q292;
            {var subQ0=sQuery(id+"F0.wireOp",EDGE,"E33");var subQ1=sQuery(id+"F0.wireOp",EDGE,"E12");var subQ2=makeQuery(id+"F0.imprint","INTERSECT",VERTEX,{"derivedFrom":[subQ1,subQ0]});Q292=makeQuery(id+"F0.imprint","IMPRINT",FACE,{"disambiguationData":[TD([[makeQuery(id+"F0.imprint","IMPRINT",EDGE,{"disambiguationData":[TD([[subQ2,1.0]])],"derivedFrom":subQ1}),-1.0]])]});}
            var Q293;
            {var subQ0=sQuery(id+"F0.wireOp",EDGE,"E34");var subQ1=sQuery(id+"F0.wireOp",EDGE,"E11");var subQ2=makeQuery(id+"F0.imprint","INTERSECT",VERTEX,{"derivedFrom":[subQ1,subQ0]});Q293=makeQuery(id+"F0.imprint","IMPRINT",FACE,{"disambiguationData":[TD([[makeQuery(id+"F0.imprint","IMPRINT",EDGE,{"disambiguationData":[TD([[subQ2,1.0]])],"derivedFrom":subQ1}),-1.0]])]});}
            var Q294;
            {var subQ0=sQuery(id+"F0.wireOp",EDGE,"E37");var subQ1=sQuery(id+"F0.wireOp",EDGE,"E8");var subQ2=makeQuery(id+"F0.imprint","INTERSECT",VERTEX,{"derivedFrom":[subQ1,subQ0]});Q294=makeQuery(id+"F0.imprint","IMPRINT",FACE,{"disambiguationData":[TD([[makeQuery(id+"F0.imprint","IMPRINT",EDGE,{"disambiguationData":[TD([[subQ2,1.0]])],"derivedFrom":subQ1}),-1.0]])]});}
            var Q295;
            {var subQ0=sQuery(id+"F0.wireOp",EDGE,"E38");var subQ1=sQuery(id+"F0.wireOp",EDGE,"E7");var subQ2=makeQuery(id+"F0.imprint","INTERSECT",VERTEX,{"derivedFrom":[subQ1,subQ0]});Q295=makeQuery(id+"F0.imprint","IMPRINT",FACE,{"disambiguationData":[TD([[makeQuery(id+"F0.imprint","IMPRINT",EDGE,{"disambiguationData":[TD([[subQ2,1.0]])],"derivedFrom":subQ1}),-1.0]])]});}
            extrude(context, id + "F1", {"entities" : qUnion([Q0, Q1, Q2, Q3, Q4, Q5, Q6, Q7, Q8, Q9, Q10, Q11, Q12, Q13, Q14, Q15, Q16, Q17, Q18, Q19, Q20, Q21, Q22, Q23, Q24, Q25, Q26, Q27, Q28, Q29, Q30, Q31, Q32, Q33, Q34, Q35, Q36, Q37, Q38, Q39, Q40, Q41, Q42, Q43, Q44, Q45, Q46, Q47, Q48, Q49, Q50, Q51, Q52, Q53, Q54, Q55, Q56, Q57, Q58, Q59, Q60, Q61, Q62, Q63, Q64, Q65, Q66, Q67, Q68, Q69, Q70, Q71, Q72, Q73, Q74, Q75, Q76, Q77, Q78, Q79, Q80, Q81, Q82, Q83, Q84, Q85, Q86, Q87, Q88, Q89, Q90, Q91, Q92, Q93, Q94, Q95, Q96, Q97, Q98, Q99, Q100, Q101, Q102, Q103, Q104, Q105, Q106, Q107, Q108, Q109, Q110, Q111, Q112, Q113, Q114, Q115, Q116, Q117, Q118, Q119, Q120, Q121, Q122, Q123, Q124, Q125, Q126, Q127, Q128, Q129, Q130, Q131, Q132, Q133, Q134, Q135, Q136, Q137, Q138, Q139, Q140, Q141, Q142, Q143, Q144, Q145, Q146, Q147, Q148, Q149, Q150, Q151, Q152, Q153, Q154, Q155, Q156, Q157, Q158, Q159, Q160, Q161, Q162, Q163, Q164, Q165, Q166, Q167, Q168, Q169, Q170, Q171, Q172, Q173, Q174, Q175, Q176, Q177, Q178, Q179, Q180, Q181, Q182, Q183, Q184, Q185, Q186, Q187, Q188, Q189, Q190, Q191, Q192, Q193, Q194, Q195, Q196, Q197, Q198, Q199, Q200, Q201, Q202, Q203, Q204, Q205, Q206, Q207, Q208, Q209, Q210, Q211, Q212, Q213, Q214, Q215, Q216, Q217, Q218, Q219, Q220, Q221, Q222, Q223, Q224, Q225, Q226, Q227, Q228, Q229, Q230, Q231, Q232, Q233, Q234, Q235, Q236, Q237, Q238, Q239, Q240, Q241, Q242, Q243, Q244, Q245, Q246, Q247, Q248, Q249, Q250, Q251, Q252, Q253, Q254, Q255, Q256, Q257, Q258, Q259, Q260, Q261, Q262, Q263, Q264, Q265, Q266, Q267, Q268, Q269, Q270, Q271, Q272, Q273, Q274, Q275, Q276, Q277, Q278, Q279, Q280, Q281, Q282, Q283, Q284, Q285, Q286, Q287, Q288, Q289, Q290, Q291, Q292, Q293, Q294, Q295]), "endBound" : BoundingType.SYMMETRIC, "depth" : 304.8 * mm});
        }
    });
